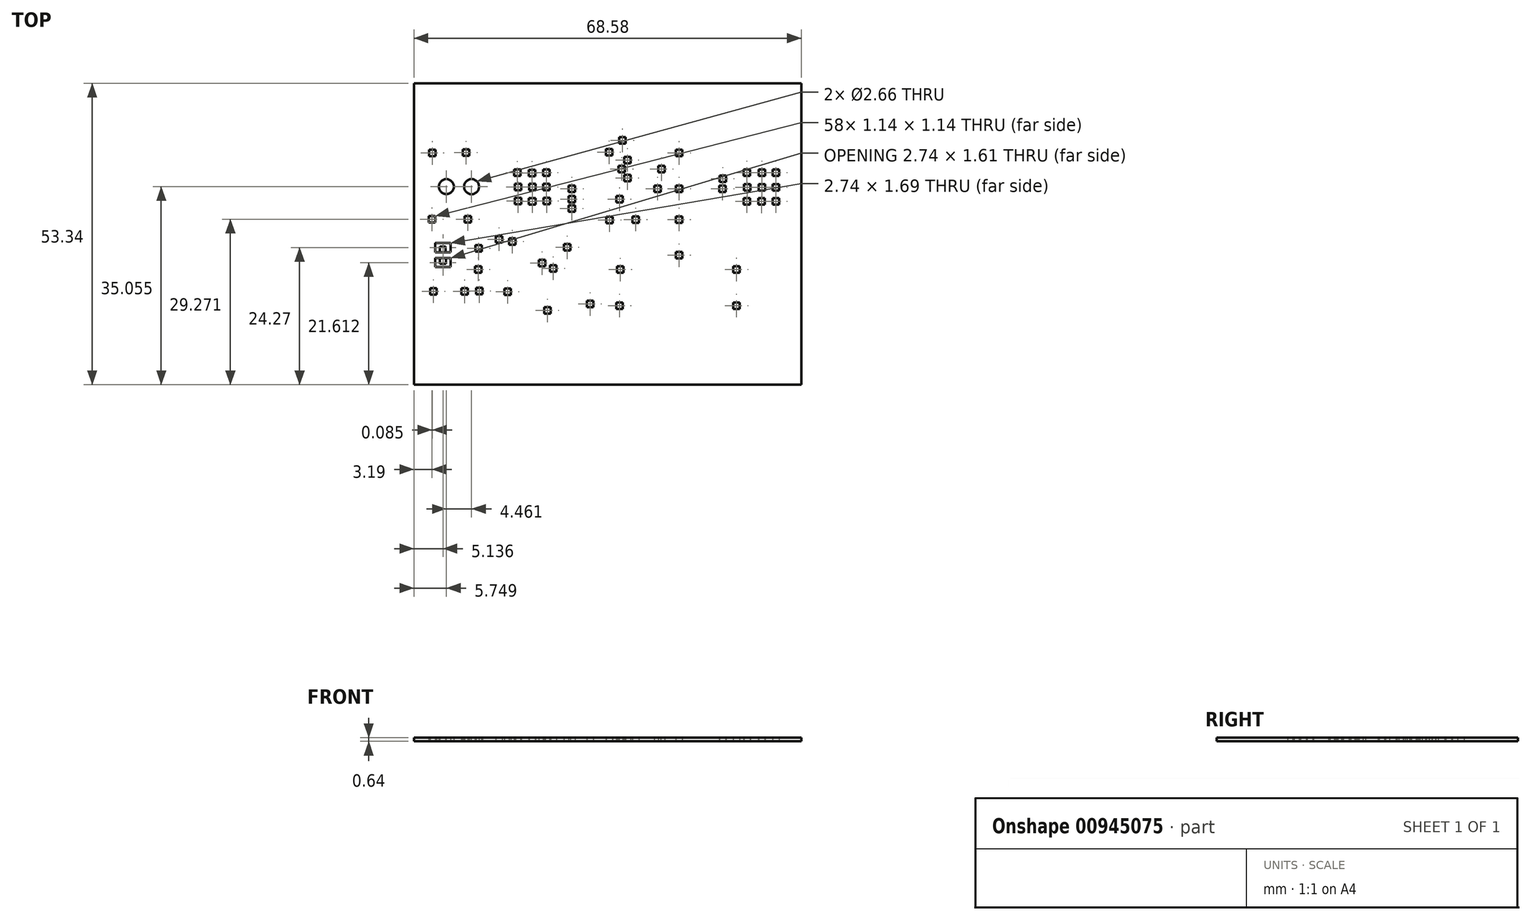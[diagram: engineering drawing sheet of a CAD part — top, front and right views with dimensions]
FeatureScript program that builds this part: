
annotation { "Feature Type Name" : "Feature", "Feature Type Description" : "" }
export const myFeature = defineFeature(function(context is Context, id is Id, definition is map)
    precondition{}
    {
        {
            var Q0;
            Q0=qCreatedBy(makeId("Top.planeOp"),FACE);
            var sketch = newSketch(context, id + "F0", { "sketchPlane" : qUnion([Q0])});
            skLineSegment(sketch, "E0.bottom", {"start": v(-43.28, 27.62) * mm, "end": v(25.3, 27.62) * mm});
            skLineSegment(sketch, "E0.top", {"start": v(-43.28, -25.72) * mm, "end": v(25.3, -25.72) * mm});
            skLineSegment(sketch, "E0.left", {"start": v(-43.28, 27.62) * mm, "end": v(-43.28, -25.72) * mm});
            skLineSegment(sketch, "E0.right", {"start": v(25.3, 27.62) * mm, "end": v(25.3, -25.72) * mm});
            skCircle(sketch, "E1", {"center": v(-37.34, -19.64) * mm, "radius": 1.71 * mm});
            skCircle(sketch, "E2", {"center": v(-37.34, -19.64) * mm, "radius": 3.05 * mm});
            skCircle(sketch, "E3", {"center": v(19.25, -19.64) * mm, "radius": 1.71 * mm});
            skCircle(sketch, "E4", {"center": v(19.25, -19.64) * mm, "radius": 3.05 * mm});
            skCircle(sketch, "E5", {"center": v(19.25, 21.73) * mm, "radius": 1.71 * mm});
            skCircle(sketch, "E6", {"center": v(19.25, 21.73) * mm, "radius": 3.05 * mm});
            skCircle(sketch, "E7", {"center": v(-37.34, 21.73) * mm, "radius": 1.71 * mm});
            skCircle(sketch, "E8", {"center": v(-37.34, 21.73) * mm, "radius": 3.05 * mm});
            skCircle(sketch, "E9", {"center": v(-37.53, 9.34) * mm, "radius": 0.82 * mm});
            skCircle(sketch, "E10", {"center": v(-37.53, 9.34) * mm, "radius": 1.33 * mm});
            skCircle(sketch, "E11", {"center": v(-33.07, 9.34) * mm, "radius": 0.83 * mm});
            skCircle(sketch, "E12", {"center": v(-33.07, 9.34) * mm, "radius": 1.33 * mm});
            skLineSegment(sketch, "E13.top", {"start": v(-39.51, -4.91) * mm, "end": v(-36.77, -4.91) * mm});
            skLineSegment(sketch, "E13.left", {"start": v(-39.51, -3.31) * mm, "end": v(-39.51, -4.91) * mm});
            skLineSegment(sketch, "E13.right", {"start": v(-36.77, -3.3) * mm, "end": v(-36.77, -4.91) * mm});
            skLineSegment(sketch, "E14.bottom", {"start": v(-38.67, -3.31) * mm, "end": v(-37.61, -3.31) * mm});
            skLineSegment(sketch, "E14.top", {"start": v(-38.67, -4.3) * mm, "end": v(-37.61, -4.3) * mm});
            skLineSegment(sketch, "E14.left", {"start": v(-38.67, -3.31) * mm, "end": v(-38.67, -4.3) * mm});
            skLineSegment(sketch, "E14.right", {"start": v(-37.61, -3.31) * mm, "end": v(-37.61, -4.3) * mm});
            skLineSegment(sketch, "E15", {"start": v(-39.51, -3.31) * mm, "end": v(-38.67, -3.31) * mm});
            skLineSegment(sketch, "E16", {"start": v(-36.77, -3.3) * mm, "end": v(-37.61, -3.31) * mm});
            skLineSegment(sketch, "E17.bottom", {"start": v(-30.19, -19.97) * mm, "end": v(-31.34, -19.97) * mm});
            skLineSegment(sketch, "E17.top", {"start": v(-30.19, -18.8) * mm, "end": v(-31.34, -18.8) * mm});
            skLineSegment(sketch, "E17.left", {"start": v(-30.19, -19.97) * mm, "end": v(-30.19, -18.8) * mm});
            skLineSegment(sketch, "E17.right", {"start": v(-31.34, -19.97) * mm, "end": v(-31.34, -18.8) * mm});
            skPoint(sketch, "E17.middle", {"position": v(-30.77, -19.39) * mm});
            skLineSegment(sketch, "E18.bottom", {"start": v(-27.6, -19.96) * mm, "end": v(-28.75, -19.96) * mm});
            skLineSegment(sketch, "E18.top", {"start": v(-27.6, -18.8) * mm, "end": v(-28.75, -18.8) * mm});
            skLineSegment(sketch, "E18.left", {"start": v(-27.6, -19.96) * mm, "end": v(-27.6, -18.8) * mm});
            skLineSegment(sketch, "E18.right", {"start": v(-28.75, -19.96) * mm, "end": v(-28.75, -18.8) * mm});
            skPoint(sketch, "E18.middle", {"position": v(-28.17, -19.39) * mm});
            skLineSegment(sketch, "E19.right", {"start": v(-29.25, -20.48) * mm, "end": v(-29.25, -18.3) * mm});
            skLineSegment(sketch, "E20.bottom", {"start": v(-24.92, -19.95) * mm, "end": v(-26.06, -19.95) * mm});
            skLineSegment(sketch, "E20.top", {"start": v(-24.92, -18.82) * mm, "end": v(-26.06, -18.82) * mm});
            skLineSegment(sketch, "E20.left", {"start": v(-24.92, -19.95) * mm, "end": v(-24.92, -18.82) * mm});
            skLineSegment(sketch, "E20.right", {"start": v(-26.06, -19.95) * mm, "end": v(-26.06, -18.82) * mm});
            skPoint(sketch, "E20.middle", {"position": v(-25.5, -19.39) * mm});
            skLineSegment(sketch, "E21.bottom", {"start": v(-22.3, -19.95) * mm, "end": v(-23.43, -19.95) * mm});
            skLineSegment(sketch, "E21.top", {"start": v(-22.3, -18.82) * mm, "end": v(-23.43, -18.82) * mm});
            skLineSegment(sketch, "E21.left", {"start": v(-22.3, -19.95) * mm, "end": v(-22.3, -18.82) * mm});
            skLineSegment(sketch, "E21.right", {"start": v(-23.43, -19.95) * mm, "end": v(-23.43, -18.82) * mm});
            skPoint(sketch, "E21.middle", {"position": v(-22.87, -19.39) * mm});
            skLineSegment(sketch, "E22.bottom", {"start": v(-19.7, -19.95) * mm, "end": v(-20.82, -19.95) * mm});
            skLineSegment(sketch, "E22.top", {"start": v(-19.7, -18.82) * mm, "end": v(-20.82, -18.82) * mm});
            skLineSegment(sketch, "E22.left", {"start": v(-19.7, -19.95) * mm, "end": v(-19.7, -18.82) * mm});
            skLineSegment(sketch, "E22.right", {"start": v(-20.82, -19.95) * mm, "end": v(-20.82, -18.82) * mm});
            skPoint(sketch, "E22.middle", {"position": v(-20.25, -19.39) * mm});
            skLineSegment(sketch, "E23.bottom", {"start": v(-17.14, -19.95) * mm, "end": v(-18.27, -19.95) * mm});
            skLineSegment(sketch, "E23.top", {"start": v(-17.14, -18.82) * mm, "end": v(-18.27, -18.82) * mm});
            skLineSegment(sketch, "E23.left", {"start": v(-17.14, -19.95) * mm, "end": v(-17.14, -18.82) * mm});
            skLineSegment(sketch, "E23.right", {"start": v(-18.27, -19.95) * mm, "end": v(-18.27, -18.82) * mm});
            skPoint(sketch, "E23.middle", {"position": v(-17.7, -19.39) * mm});
            skLineSegment(sketch, "E24.bottom", {"start": v(-14.69, -19.96) * mm, "end": v(-15.84, -19.96) * mm});
            skLineSegment(sketch, "E24.top", {"start": v(-14.69, -18.82) * mm, "end": v(-15.84, -18.82) * mm});
            skLineSegment(sketch, "E24.left", {"start": v(-14.69, -19.96) * mm, "end": v(-14.69, -18.82) * mm});
            skLineSegment(sketch, "E24.right", {"start": v(-15.84, -19.96) * mm, "end": v(-15.84, -18.82) * mm});
            skPoint(sketch, "E24.middle", {"position": v(-15.26, -19.39) * mm});
            skLineSegment(sketch, "E25.bottom", {"start": v(-12.26, -19.96) * mm, "end": v(-13.41, -19.96) * mm});
            skLineSegment(sketch, "E25.top", {"start": v(-12.26, -18.82) * mm, "end": v(-13.41, -18.82) * mm});
            skLineSegment(sketch, "E25.left", {"start": v(-12.26, -19.96) * mm, "end": v(-12.26, -18.82) * mm});
            skLineSegment(sketch, "E25.right", {"start": v(-13.41, -19.96) * mm, "end": v(-13.41, -18.82) * mm});
            skPoint(sketch, "E25.middle", {"position": v(-12.84, -19.39) * mm});
            skLineSegment(sketch, "E26.bottom", {"start": v(-30.19, -18.3) * mm, "end": v(-31.95, -18.3) * mm});
            skLineSegment(sketch, "E26.top", {"start": v(-30.19, -20.46) * mm, "end": v(-31.95, -20.46) * mm});
            skLineSegment(sketch, "E26.left", {"start": v(-30.19, -18.3) * mm, "end": v(-30.19, -20.46) * mm});
            skLineSegment(sketch, "E26.right", {"start": v(-31.95, -18.3) * mm, "end": v(-31.95, -20.46) * mm});
            skLineSegment(sketch, "E27", {"start": v(-27.6, -18.8) * mm, "end": v(-27.6, -18.3) * mm});
            skLineSegment(sketch, "E28", {"start": v(-27.6, -18.3) * mm, "end": v(-29.25, -18.3) * mm});
            skLineSegment(sketch, "E29", {"start": v(-27.6, -19.96) * mm, "end": v(-27.6, -20.47) * mm});
            skLineSegment(sketch, "E30", {"start": v(-27.6, -20.47) * mm, "end": v(-29.25, -20.48) * mm});
            skLineSegment(sketch, "E31", {"start": v(-24.92, -18.82) * mm, "end": v(-24.92, -18.32) * mm});
            skLineSegment(sketch, "E32", {"start": v(-24.92, -18.32) * mm, "end": v(-26.56, -18.32) * mm});
            skLineSegment(sketch, "E33", {"start": v(-26.56, -18.32) * mm, "end": v(-26.56, -20.47) * mm});
            skLineSegment(sketch, "E34", {"start": v(-26.56, -20.47) * mm, "end": v(-24.92, -20.47) * mm});
            skLineSegment(sketch, "E35", {"start": v(-24.92, -20.47) * mm, "end": v(-24.92, -19.95) * mm});
            skLineSegment(sketch, "E36", {"start": v(-22.3, -18.82) * mm, "end": v(-22.3, -18.32) * mm});
            skLineSegment(sketch, "E37", {"start": v(-22.3, -18.32) * mm, "end": v(-23.96, -18.32) * mm});
            skLineSegment(sketch, "E38", {"start": v(-23.96, -18.32) * mm, "end": v(-23.96, -20.47) * mm});
            skLineSegment(sketch, "E39", {"start": v(-23.96, -20.47) * mm, "end": v(-22.3, -20.47) * mm});
            skLineSegment(sketch, "E40", {"start": v(-22.3, -20.47) * mm, "end": v(-22.3, -19.95) * mm});
            skLineSegment(sketch, "E41", {"start": v(-19.7, -18.82) * mm, "end": v(-19.7, -18.32) * mm});
            skLineSegment(sketch, "E42", {"start": v(-19.7, -18.32) * mm, "end": v(-21.35, -18.32) * mm});
            skLineSegment(sketch, "E43", {"start": v(-21.35, -18.32) * mm, "end": v(-21.35, -20.46) * mm});
            skLineSegment(sketch, "E44", {"start": v(-21.35, -20.46) * mm, "end": v(-19.7, -20.46) * mm});
            skLineSegment(sketch, "E45", {"start": v(-19.7, -20.46) * mm, "end": v(-19.7, -19.95) * mm});
            skLineSegment(sketch, "E46", {"start": v(-17.14, -18.82) * mm, "end": v(-17.14, -18.3) * mm});
            skLineSegment(sketch, "E47", {"start": v(-17.14, -18.3) * mm, "end": v(-18.8, -18.3) * mm});
            skLineSegment(sketch, "E48", {"start": v(-18.8, -18.3) * mm, "end": v(-18.8, -20.46) * mm});
            skLineSegment(sketch, "E49", {"start": v(-18.8, -20.46) * mm, "end": v(-17.14, -20.46) * mm});
            skLineSegment(sketch, "E50", {"start": v(-17.14, -20.46) * mm, "end": v(-17.14, -19.95) * mm});
            skLineSegment(sketch, "E51", {"start": v(-14.69, -18.82) * mm, "end": v(-14.69, -18.3) * mm});
            skLineSegment(sketch, "E52", {"start": v(-14.69, -18.3) * mm, "end": v(-16.33, -18.3) * mm});
            skLineSegment(sketch, "E53", {"start": v(-16.33, -18.3) * mm, "end": v(-16.33, -20.47) * mm});
            skLineSegment(sketch, "E54", {"start": v(-16.33, -20.47) * mm, "end": v(-14.69, -20.47) * mm});
            skLineSegment(sketch, "E55", {"start": v(-14.69, -20.47) * mm, "end": v(-14.69, -19.96) * mm});
            skLineSegment(sketch, "E56", {"start": v(-12.26, -18.82) * mm, "end": v(-12.26, -18.31) * mm});
            skLineSegment(sketch, "E57", {"start": v(-12.26, -18.31) * mm, "end": v(-13.91, -18.31) * mm});
            skLineSegment(sketch, "E58", {"start": v(-13.91, -18.31) * mm, "end": v(-13.91, -20.47) * mm});
            skLineSegment(sketch, "E59", {"start": v(-13.91, -20.47) * mm, "end": v(-12.26, -20.47) * mm});
            skLineSegment(sketch, "E60", {"start": v(-12.26, -20.47) * mm, "end": v(-12.26, -19.96) * mm});
            skLineSegment(sketch, "E61.bottom", {"start": v(-9.74, -19.95) * mm, "end": v(-10.89, -19.95) * mm});
            skLineSegment(sketch, "E61.top", {"start": v(-9.74, -18.82) * mm, "end": v(-10.89, -18.82) * mm});
            skLineSegment(sketch, "E61.left", {"start": v(-9.74, -19.95) * mm, "end": v(-9.74, -18.82) * mm});
            skLineSegment(sketch, "E61.right", {"start": v(-10.89, -19.95) * mm, "end": v(-10.89, -18.82) * mm});
            skPoint(sketch, "E61.middle", {"position": v(-10.31, -19.39) * mm});
            skPoint(sketch, "E62.middle", {"position": v(-7.76, -19.39) * mm});
            skLineSegment(sketch, "E63.bottom", {"start": v(-7.19, -19.96) * mm, "end": v(-8.34, -19.96) * mm});
            skLineSegment(sketch, "E63.top", {"start": v(-7.19, -18.81) * mm, "end": v(-8.34, -18.81) * mm});
            skLineSegment(sketch, "E63.left", {"start": v(-7.19, -19.96) * mm, "end": v(-7.19, -18.81) * mm});
            skLineSegment(sketch, "E63.right", {"start": v(-8.34, -19.96) * mm, "end": v(-8.34, -18.81) * mm});
            skLineSegment(sketch, "E64.bottom", {"start": v(-4.68, -19.96) * mm, "end": v(-5.82, -19.96) * mm});
            skLineSegment(sketch, "E64.top", {"start": v(-4.68, -18.81) * mm, "end": v(-5.82, -18.81) * mm});
            skLineSegment(sketch, "E64.left", {"start": v(-4.68, -19.96) * mm, "end": v(-4.68, -18.81) * mm});
            skLineSegment(sketch, "E64.right", {"start": v(-5.82, -19.96) * mm, "end": v(-5.82, -18.81) * mm});
            skPoint(sketch, "E64.middle", {"position": v(-5.25, -19.39) * mm});
            skLineSegment(sketch, "E65.bottom", {"start": v(-2.14, -19.96) * mm, "end": v(-3.29, -19.96) * mm});
            skLineSegment(sketch, "E65.top", {"start": v(-2.14, -18.81) * mm, "end": v(-3.29, -18.81) * mm});
            skLineSegment(sketch, "E65.left", {"start": v(-2.14, -19.96) * mm, "end": v(-2.14, -18.81) * mm});
            skLineSegment(sketch, "E65.right", {"start": v(-3.29, -19.96) * mm, "end": v(-3.29, -18.81) * mm});
            skPoint(sketch, "E65.middle", {"position": v(-2.71, -19.39) * mm});
            skLineSegment(sketch, "E66.bottom", {"start": v(0.38, -19.96) * mm, "end": v(-0.76, -19.96) * mm});
            skLineSegment(sketch, "E66.top", {"start": v(0.38, -18.81) * mm, "end": v(-0.76, -18.81) * mm});
            skLineSegment(sketch, "E66.left", {"start": v(0.38, -19.96) * mm, "end": v(0.38, -18.81) * mm});
            skLineSegment(sketch, "E66.right", {"start": v(-0.76, -19.96) * mm, "end": v(-0.76, -18.81) * mm});
            skPoint(sketch, "E66.middle", {"position": v(-0.19, -19.39) * mm});
            skLineSegment(sketch, "E67.bottom", {"start": v(2.91, -19.96) * mm, "end": v(1.78, -19.96) * mm});
            skLineSegment(sketch, "E67.top", {"start": v(2.91, -18.81) * mm, "end": v(1.78, -18.81) * mm});
            skLineSegment(sketch, "E67.left", {"start": v(2.91, -19.96) * mm, "end": v(2.91, -18.81) * mm});
            skLineSegment(sketch, "E67.right", {"start": v(1.78, -19.96) * mm, "end": v(1.78, -18.81) * mm});
            skPoint(sketch, "E67.middle", {"position": v(2.35, -19.39) * mm});
            skLineSegment(sketch, "E68.bottom", {"start": v(8.82, -19.96) * mm, "end": v(7.68, -19.96) * mm});
            skLineSegment(sketch, "E68.top", {"start": v(8.82, -18.81) * mm, "end": v(7.68, -18.81) * mm});
            skLineSegment(sketch, "E68.left", {"start": v(8.82, -19.96) * mm, "end": v(8.82, -18.81) * mm});
            skLineSegment(sketch, "E68.right", {"start": v(7.68, -19.96) * mm, "end": v(7.68, -18.81) * mm});
            skPoint(sketch, "E68.middle", {"position": v(8.25, -19.39) * mm});
            skLineSegment(sketch, "E69.bottom", {"start": v(11.35, -19.96) * mm, "end": v(10.21, -19.96) * mm});
            skLineSegment(sketch, "E69.top", {"start": v(11.35, -18.81) * mm, "end": v(10.21, -18.81) * mm});
            skLineSegment(sketch, "E69.left", {"start": v(11.35, -19.96) * mm, "end": v(11.35, -18.81) * mm});
            skLineSegment(sketch, "E69.right", {"start": v(10.21, -19.96) * mm, "end": v(10.21, -18.81) * mm});
            skPoint(sketch, "E69.middle", {"position": v(10.78, -19.39) * mm});
            skPoint(sketch, "E70.middle", {"position": v(13.33, -19.39) * mm});
            skLineSegment(sketch, "E71.bottom", {"start": v(13.9, -19.96) * mm, "end": v(12.75, -19.96) * mm});
            skLineSegment(sketch, "E71.top", {"start": v(13.9, -18.82) * mm, "end": v(12.75, -18.82) * mm});
            skLineSegment(sketch, "E71.left", {"start": v(13.9, -19.96) * mm, "end": v(13.9, -18.82) * mm});
            skLineSegment(sketch, "E71.right", {"start": v(12.75, -19.96) * mm, "end": v(12.75, -18.82) * mm});
            skLineSegment(sketch, "E72", {"start": v(-9.74, -18.82) * mm, "end": v(-9.74, -18.3) * mm});
            skLineSegment(sketch, "E73", {"start": v(-9.74, -18.3) * mm, "end": v(-11.39, -18.3) * mm});
            skLineSegment(sketch, "E74", {"start": v(-11.39, -18.3) * mm, "end": v(-11.39, -20.46) * mm});
            skLineSegment(sketch, "E75", {"start": v(-11.39, -20.46) * mm, "end": v(-9.74, -20.46) * mm});
            skLineSegment(sketch, "E76", {"start": v(-9.74, -20.46) * mm, "end": v(-9.74, -19.95) * mm});
            skLineSegment(sketch, "E77", {"start": v(-7.19, -18.81) * mm, "end": v(-7.19, -18.3) * mm});
            skLineSegment(sketch, "E78", {"start": v(-7.19, -18.3) * mm, "end": v(-8.84, -18.3) * mm});
            skLineSegment(sketch, "E79", {"start": v(-8.84, -18.3) * mm, "end": v(-8.84, -20.46) * mm});
            skLineSegment(sketch, "E80", {"start": v(-8.84, -20.46) * mm, "end": v(-7.19, -20.46) * mm});
            skLineSegment(sketch, "E81", {"start": v(-7.19, -20.46) * mm, "end": v(-7.19, -19.96) * mm});
            skLineSegment(sketch, "E82", {"start": v(-4.68, -18.81) * mm, "end": v(-4.68, -18.3) * mm});
            skLineSegment(sketch, "E83", {"start": v(-4.68, -18.3) * mm, "end": v(-6.32, -18.3) * mm});
            skLineSegment(sketch, "E84", {"start": v(-6.32, -18.3) * mm, "end": v(-6.32, -20.46) * mm});
            skLineSegment(sketch, "E85", {"start": v(-6.32, -20.46) * mm, "end": v(-4.68, -20.46) * mm});
            skLineSegment(sketch, "E86", {"start": v(-4.68, -20.46) * mm, "end": v(-4.68, -19.96) * mm});
            skLineSegment(sketch, "E87", {"start": v(-2.14, -18.81) * mm, "end": v(-2.14, -18.3) * mm});
            skLineSegment(sketch, "E88", {"start": v(-2.14, -18.3) * mm, "end": v(-3.8, -18.3) * mm});
            skLineSegment(sketch, "E89", {"start": v(-3.8, -18.3) * mm, "end": v(-3.78, -20.45) * mm});
            skLineSegment(sketch, "E90", {"start": v(-3.78, -20.45) * mm, "end": v(-2.14, -20.45) * mm});
            skLineSegment(sketch, "E91", {"start": v(-2.14, -20.45) * mm, "end": v(-2.14, -19.96) * mm});
            skLineSegment(sketch, "E92", {"start": v(0.38, -18.81) * mm, "end": v(0.38, -18.3) * mm});
            skLineSegment(sketch, "E93", {"start": v(0.38, -18.3) * mm, "end": v(-1.26, -18.3) * mm});
            skLineSegment(sketch, "E94", {"start": v(-1.26, -18.3) * mm, "end": v(-1.26, -20.46) * mm});
            skLineSegment(sketch, "E95", {"start": v(-1.26, -20.46) * mm, "end": v(0.38, -20.46) * mm});
            skLineSegment(sketch, "E96", {"start": v(0.38, -20.46) * mm, "end": v(0.38, -19.96) * mm});
            skLineSegment(sketch, "E97", {"start": v(2.91, -18.81) * mm, "end": v(2.91, -18.31) * mm});
            skLineSegment(sketch, "E98", {"start": v(2.91, -18.31) * mm, "end": v(1.27, -18.31) * mm});
            skLineSegment(sketch, "E99", {"start": v(1.27, -18.31) * mm, "end": v(1.27, -20.48) * mm});
            skLineSegment(sketch, "E100", {"start": v(1.27, -20.48) * mm, "end": v(2.91, -20.48) * mm});
            skLineSegment(sketch, "E101", {"start": v(2.91, -20.48) * mm, "end": v(2.91, -19.96) * mm});
            skLineSegment(sketch, "E102", {"start": v(8.82, -18.81) * mm, "end": v(8.82, -18.3) * mm});
            skLineSegment(sketch, "E103", {"start": v(8.82, -18.3) * mm, "end": v(7.17, -18.3) * mm});
            skLineSegment(sketch, "E104", {"start": v(7.17, -18.3) * mm, "end": v(7.17, -20.46) * mm});
            skLineSegment(sketch, "E105", {"start": v(7.17, -20.46) * mm, "end": v(8.82, -20.46) * mm});
            skLineSegment(sketch, "E106", {"start": v(8.82, -20.46) * mm, "end": v(8.82, -19.96) * mm});
            skLineSegment(sketch, "E107", {"start": v(11.35, -18.81) * mm, "end": v(11.35, -18.3) * mm});
            skLineSegment(sketch, "E108", {"start": v(11.35, -18.3) * mm, "end": v(9.7, -18.3) * mm});
            skLineSegment(sketch, "E109", {"start": v(9.7, -18.3) * mm, "end": v(9.7, -20.46) * mm});
            skLineSegment(sketch, "E110", {"start": v(9.7, -20.46) * mm, "end": v(11.35, -20.46) * mm});
            skLineSegment(sketch, "E111", {"start": v(11.35, -20.46) * mm, "end": v(11.35, -19.96) * mm});
            skLineSegment(sketch, "E112", {"start": v(13.9, -18.82) * mm, "end": v(13.9, -18.31) * mm});
            skLineSegment(sketch, "E113", {"start": v(13.9, -18.31) * mm, "end": v(12.25, -18.31) * mm});
            skLineSegment(sketch, "E114", {"start": v(12.25, -18.31) * mm, "end": v(12.25, -20.46) * mm});
            skLineSegment(sketch, "E115", {"start": v(12.25, -20.46) * mm, "end": v(13.9, -20.46) * mm});
            skLineSegment(sketch, "E116", {"start": v(13.9, -20.46) * mm, "end": v(13.9, -19.96) * mm});
            skLineSegment(sketch, "E117.bottom", {"start": v(11.36, 20.51) * mm, "end": v(10.21, 20.51) * mm});
            skLineSegment(sketch, "E117.top", {"start": v(11.36, 21.64) * mm, "end": v(10.21, 21.64) * mm});
            skLineSegment(sketch, "E117.left", {"start": v(11.36, 20.51) * mm, "end": v(11.36, 21.64) * mm});
            skLineSegment(sketch, "E117.right", {"start": v(10.21, 20.51) * mm, "end": v(10.21, 21.64) * mm});
            skPoint(sketch, "E117.middle", {"position": v(10.78, 21.08) * mm});
            skLineSegment(sketch, "E118.bottom", {"start": v(8.82, 20.51) * mm, "end": v(7.68, 20.51) * mm});
            skLineSegment(sketch, "E118.top", {"start": v(8.82, 21.64) * mm, "end": v(7.68, 21.64) * mm});
            skLineSegment(sketch, "E118.left", {"start": v(8.82, 20.51) * mm, "end": v(8.82, 21.64) * mm});
            skLineSegment(sketch, "E118.right", {"start": v(7.68, 20.51) * mm, "end": v(7.68, 21.64) * mm});
            skPoint(sketch, "E118.middle", {"position": v(8.25, 21.08) * mm});
            skLineSegment(sketch, "E119.bottom", {"start": v(2.92, 20.51) * mm, "end": v(1.77, 20.51) * mm});
            skLineSegment(sketch, "E119.top", {"start": v(2.92, 21.64) * mm, "end": v(1.77, 21.64) * mm});
            skLineSegment(sketch, "E119.left", {"start": v(2.92, 20.51) * mm, "end": v(2.92, 21.64) * mm});
            skLineSegment(sketch, "E119.right", {"start": v(1.77, 20.51) * mm, "end": v(1.77, 21.64) * mm});
            skPoint(sketch, "E119.middle", {"position": v(2.35, 21.08) * mm});
            skLineSegment(sketch, "E120.bottom", {"start": v(0.39, 20.5) * mm, "end": v(-0.76, 20.5) * mm});
            skLineSegment(sketch, "E120.top", {"start": v(0.39, 21.64) * mm, "end": v(-0.76, 21.64) * mm});
            skLineSegment(sketch, "E120.left", {"start": v(0.39, 20.5) * mm, "end": v(0.39, 21.64) * mm});
            skLineSegment(sketch, "E120.right", {"start": v(-0.76, 20.5) * mm, "end": v(-0.76, 21.64) * mm});
            skPoint(sketch, "E120.middle", {"position": v(-0.19, 21.08) * mm});
            skLineSegment(sketch, "E121.bottom", {"start": v(-2.14, 20.5) * mm, "end": v(-3.29, 20.5) * mm});
            skLineSegment(sketch, "E121.top", {"start": v(-2.14, 21.65) * mm, "end": v(-3.29, 21.65) * mm});
            skLineSegment(sketch, "E121.left", {"start": v(-2.14, 20.5) * mm, "end": v(-2.14, 21.65) * mm});
            skLineSegment(sketch, "E121.right", {"start": v(-3.29, 20.5) * mm, "end": v(-3.29, 21.65) * mm});
            skPoint(sketch, "E121.middle", {"position": v(-2.71, 21.08) * mm});
            skLineSegment(sketch, "E122.bottom", {"start": v(-4.68, 20.5) * mm, "end": v(-5.82, 20.5) * mm});
            skLineSegment(sketch, "E122.top", {"start": v(-4.68, 21.65) * mm, "end": v(-5.82, 21.65) * mm});
            skLineSegment(sketch, "E122.left", {"start": v(-4.68, 20.5) * mm, "end": v(-4.68, 21.65) * mm});
            skLineSegment(sketch, "E122.right", {"start": v(-5.82, 20.5) * mm, "end": v(-5.82, 21.65) * mm});
            skPoint(sketch, "E122.middle", {"position": v(-5.25, 21.08) * mm});
            skLineSegment(sketch, "E123.bottom", {"start": v(-7.2, 20.5) * mm, "end": v(-8.33, 20.5) * mm});
            skLineSegment(sketch, "E123.top", {"start": v(-7.2, 21.65) * mm, "end": v(-8.33, 21.65) * mm});
            skLineSegment(sketch, "E123.left", {"start": v(-7.2, 20.5) * mm, "end": v(-7.2, 21.65) * mm});
            skLineSegment(sketch, "E123.right", {"start": v(-8.33, 20.5) * mm, "end": v(-8.33, 21.65) * mm});
            skPoint(sketch, "E123.middle", {"position": v(-7.76, 21.08) * mm});
            skLineSegment(sketch, "E124.bottom", {"start": v(-9.74, 20.5) * mm, "end": v(-10.88, 20.5) * mm});
            skLineSegment(sketch, "E124.top", {"start": v(-9.74, 21.64) * mm, "end": v(-10.88, 21.64) * mm});
            skLineSegment(sketch, "E124.left", {"start": v(-9.74, 20.5) * mm, "end": v(-9.74, 21.64) * mm});
            skLineSegment(sketch, "E124.right", {"start": v(-10.88, 20.5) * mm, "end": v(-10.88, 21.64) * mm});
            skPoint(sketch, "E124.middle", {"position": v(-10.31, 21.08) * mm});
            skLineSegment(sketch, "E125.bottom", {"start": v(-12.26, 20.51) * mm, "end": v(-13.41, 20.51) * mm});
            skLineSegment(sketch, "E125.top", {"start": v(-12.26, 21.64) * mm, "end": v(-13.41, 21.64) * mm});
            skLineSegment(sketch, "E125.left", {"start": v(-12.26, 20.51) * mm, "end": v(-12.26, 21.64) * mm});
            skLineSegment(sketch, "E125.right", {"start": v(-13.41, 20.51) * mm, "end": v(-13.41, 21.64) * mm});
            skPoint(sketch, "E125.middle", {"position": v(-12.84, 21.08) * mm});
            skLineSegment(sketch, "E126.bottom", {"start": v(-14.7, 20.5) * mm, "end": v(-15.83, 20.5) * mm});
            skLineSegment(sketch, "E126.top", {"start": v(-14.7, 21.65) * mm, "end": v(-15.83, 21.65) * mm});
            skLineSegment(sketch, "E126.left", {"start": v(-14.7, 20.5) * mm, "end": v(-14.7, 21.65) * mm});
            skLineSegment(sketch, "E126.right", {"start": v(-15.83, 20.5) * mm, "end": v(-15.83, 21.65) * mm});
            skPoint(sketch, "E126.middle", {"position": v(-15.26, 21.08) * mm});
            skLineSegment(sketch, "E127.bottom", {"start": v(-17.13, 20.5) * mm, "end": v(-18.28, 20.5) * mm});
            skLineSegment(sketch, "E127.top", {"start": v(-17.13, 21.65) * mm, "end": v(-18.28, 21.65) * mm});
            skLineSegment(sketch, "E127.left", {"start": v(-17.13, 20.5) * mm, "end": v(-17.13, 21.65) * mm});
            skLineSegment(sketch, "E127.right", {"start": v(-18.28, 20.5) * mm, "end": v(-18.28, 21.65) * mm});
            skPoint(sketch, "E127.middle", {"position": v(-17.7, 21.08) * mm});
            skLineSegment(sketch, "E128.bottom", {"start": v(-19.69, 20.5) * mm, "end": v(-20.82, 20.5) * mm});
            skLineSegment(sketch, "E128.top", {"start": v(-19.69, 21.65) * mm, "end": v(-20.82, 21.65) * mm});
            skLineSegment(sketch, "E128.left", {"start": v(-19.69, 20.5) * mm, "end": v(-19.69, 21.65) * mm});
            skLineSegment(sketch, "E128.right", {"start": v(-20.82, 20.5) * mm, "end": v(-20.82, 21.65) * mm});
            skPoint(sketch, "E128.middle", {"position": v(-20.25, 21.08) * mm});
            skLineSegment(sketch, "E129.bottom", {"start": v(-22.29, 20.5) * mm, "end": v(-23.44, 20.5) * mm});
            skLineSegment(sketch, "E129.top", {"start": v(-22.29, 21.65) * mm, "end": v(-23.44, 21.65) * mm});
            skLineSegment(sketch, "E129.left", {"start": v(-22.29, 20.5) * mm, "end": v(-22.29, 21.65) * mm});
            skLineSegment(sketch, "E129.right", {"start": v(-23.44, 20.5) * mm, "end": v(-23.44, 21.65) * mm});
            skPoint(sketch, "E129.middle", {"position": v(-22.87, 21.08) * mm});
            skLineSegment(sketch, "E130.bottom", {"start": v(-24.92, 20.5) * mm, "end": v(-26.06, 20.5) * mm});
            skLineSegment(sketch, "E130.top", {"start": v(-24.92, 21.65) * mm, "end": v(-26.06, 21.65) * mm});
            skLineSegment(sketch, "E130.left", {"start": v(-24.92, 20.5) * mm, "end": v(-24.92, 21.65) * mm});
            skLineSegment(sketch, "E130.right", {"start": v(-26.06, 20.5) * mm, "end": v(-26.06, 21.65) * mm});
            skPoint(sketch, "E130.middle", {"position": v(-25.5, 21.08) * mm});
            skLineSegment(sketch, "E131.bottom", {"start": v(-27.6, 20.5) * mm, "end": v(-28.74, 20.5) * mm});
            skLineSegment(sketch, "E131.top", {"start": v(-27.6, 21.65) * mm, "end": v(-28.74, 21.65) * mm});
            skLineSegment(sketch, "E131.left", {"start": v(-27.6, 20.5) * mm, "end": v(-27.6, 21.65) * mm});
            skLineSegment(sketch, "E131.right", {"start": v(-28.74, 20.5) * mm, "end": v(-28.74, 21.65) * mm});
            skPoint(sketch, "E131.middle", {"position": v(-28.17, 21.08) * mm});
            skLineSegment(sketch, "E132.bottom", {"start": v(13.9, 20.5) * mm, "end": v(12.76, 20.5) * mm});
            skLineSegment(sketch, "E132.top", {"start": v(13.9, 21.65) * mm, "end": v(12.76, 21.65) * mm});
            skLineSegment(sketch, "E132.left", {"start": v(13.9, 20.5) * mm, "end": v(13.9, 21.65) * mm});
            skLineSegment(sketch, "E132.right", {"start": v(12.76, 20.5) * mm, "end": v(12.76, 21.65) * mm});
            skPoint(sketch, "E132.middle", {"position": v(13.33, 21.08) * mm});
            skLineSegment(sketch, "E133", {"start": v(13.9, 21.65) * mm, "end": v(13.9, 22.15) * mm});
            skLineSegment(sketch, "E134", {"start": v(13.9, 22.15) * mm, "end": v(12.25, 22.15) * mm});
            skLineSegment(sketch, "E135", {"start": v(12.25, 22.15) * mm, "end": v(12.25, 19.98) * mm});
            skLineSegment(sketch, "E136", {"start": v(12.25, 19.98) * mm, "end": v(13.9, 19.98) * mm});
            skLineSegment(sketch, "E137", {"start": v(13.9, 19.98) * mm, "end": v(13.9, 20.5) * mm});
            skLineSegment(sketch, "E138.bottom", {"start": v(-30.2, 20.5) * mm, "end": v(-31.34, 20.5) * mm});
            skLineSegment(sketch, "E138.top", {"start": v(-30.2, 21.64) * mm, "end": v(-31.34, 21.64) * mm});
            skLineSegment(sketch, "E138.left", {"start": v(-30.2, 20.5) * mm, "end": v(-30.2, 21.64) * mm});
            skLineSegment(sketch, "E138.right", {"start": v(-31.34, 20.5) * mm, "end": v(-31.34, 21.64) * mm});
            skPoint(sketch, "E138.middle", {"position": v(-30.77, 21.08) * mm});
            skLineSegment(sketch, "E139", {"start": v(-30.2, 21.64) * mm, "end": v(-30.2, 22.15) * mm});
            skLineSegment(sketch, "E140", {"start": v(-30.2, 22.15) * mm, "end": v(-31.85, 22.15) * mm});
            skLineSegment(sketch, "E141", {"start": v(-31.85, 22.15) * mm, "end": v(-31.85, 19.99) * mm});
            skLineSegment(sketch, "E142", {"start": v(-31.85, 19.99) * mm, "end": v(-30.2, 19.99) * mm});
            skLineSegment(sketch, "E143", {"start": v(-30.2, 19.99) * mm, "end": v(-30.2, 20.5) * mm});
            skLineSegment(sketch, "E144", {"start": v(-27.6, 21.65) * mm, "end": v(-27.6, 22.15) * mm});
            skLineSegment(sketch, "E145", {"start": v(-27.6, 22.15) * mm, "end": v(-29.25, 22.15) * mm});
            skLineSegment(sketch, "E146", {"start": v(-29.25, 22.15) * mm, "end": v(-29.25, 20) * mm});
            skLineSegment(sketch, "E147", {"start": v(-29.25, 20) * mm, "end": v(-27.6, 20) * mm});
            skLineSegment(sketch, "E148", {"start": v(-27.6, 20) * mm, "end": v(-27.6, 20.5) * mm});
            skLineSegment(sketch, "E149", {"start": v(-24.92, 21.65) * mm, "end": v(-24.92, 22.15) * mm});
            skLineSegment(sketch, "E150", {"start": v(-24.92, 22.15) * mm, "end": v(-26.57, 22.15) * mm});
            skLineSegment(sketch, "E151", {"start": v(-26.57, 22.15) * mm, "end": v(-26.57, 19.98) * mm});
            skLineSegment(sketch, "E152", {"start": v(-26.57, 19.98) * mm, "end": v(-24.92, 19.98) * mm});
            skLineSegment(sketch, "E153", {"start": v(-24.92, 19.98) * mm, "end": v(-24.92, 20.5) * mm});
            skLineSegment(sketch, "E154", {"start": v(-22.29, 21.65) * mm, "end": v(-22.29, 22.15) * mm});
            skLineSegment(sketch, "E155", {"start": v(-22.29, 22.15) * mm, "end": v(-23.93, 22.15) * mm});
            skLineSegment(sketch, "E156", {"start": v(-23.93, 22.15) * mm, "end": v(-23.93, 19.98) * mm});
            skLineSegment(sketch, "E157", {"start": v(-23.93, 19.98) * mm, "end": v(-22.29, 19.98) * mm});
            skLineSegment(sketch, "E158", {"start": v(-22.29, 19.98) * mm, "end": v(-22.29, 20.5) * mm});
            skLineSegment(sketch, "E159", {"start": v(-19.69, 21.65) * mm, "end": v(-19.69, 22.14) * mm});
            skLineSegment(sketch, "E160", {"start": v(-19.69, 22.14) * mm, "end": v(-21.33, 22.14) * mm});
            skLineSegment(sketch, "E161", {"start": v(-21.33, 22.14) * mm, "end": v(-21.33, 19.99) * mm});
            skLineSegment(sketch, "E162", {"start": v(-21.33, 19.99) * mm, "end": v(-19.69, 19.99) * mm});
            skLineSegment(sketch, "E163", {"start": v(-19.69, 19.99) * mm, "end": v(-19.69, 20.5) * mm});
            skLineSegment(sketch, "E164", {"start": v(-17.13, 21.65) * mm, "end": v(-17.13, 22.15) * mm});
            skLineSegment(sketch, "E165", {"start": v(-17.13, 22.15) * mm, "end": v(-18.76, 22.15) * mm});
            skLineSegment(sketch, "E166", {"start": v(-18.76, 22.15) * mm, "end": v(-18.76, 19.98) * mm});
            skLineSegment(sketch, "E167", {"start": v(-18.76, 19.98) * mm, "end": v(-17.13, 19.98) * mm});
            skLineSegment(sketch, "E168", {"start": v(-17.13, 19.98) * mm, "end": v(-17.13, 20.5) * mm});
            skLineSegment(sketch, "E169", {"start": v(-14.7, 21.65) * mm, "end": v(-14.7, 22.17) * mm});
            skLineSegment(sketch, "E170", {"start": v(-14.7, 22.17) * mm, "end": v(-16.33, 22.17) * mm});
            skLineSegment(sketch, "E171", {"start": v(-16.33, 22.17) * mm, "end": v(-16.33, 20.02) * mm});
            skLineSegment(sketch, "E172", {"start": v(-16.33, 20.02) * mm, "end": v(-14.7, 20.02) * mm});
            skLineSegment(sketch, "E173", {"start": v(-14.7, 20.02) * mm, "end": v(-14.7, 20.5) * mm});
            skLineSegment(sketch, "E174", {"start": v(-12.26, 21.64) * mm, "end": v(-12.26, 22.14) * mm});
            skLineSegment(sketch, "E175", {"start": v(-12.26, 22.14) * mm, "end": v(-13.9, 22.14) * mm});
            skLineSegment(sketch, "E176", {"start": v(-13.9, 22.14) * mm, "end": v(-13.9, 20) * mm});
            skLineSegment(sketch, "E177", {"start": v(-13.9, 20) * mm, "end": v(-12.26, 20) * mm});
            skLineSegment(sketch, "E178", {"start": v(-12.26, 20) * mm, "end": v(-12.26, 20.51) * mm});
            skLineSegment(sketch, "E179", {"start": v(-9.74, 21.64) * mm, "end": v(-9.74, 22.16) * mm});
            skLineSegment(sketch, "E180", {"start": v(-9.74, 22.16) * mm, "end": v(-11.4, 22.16) * mm});
            skLineSegment(sketch, "E181", {"start": v(-11.4, 22.16) * mm, "end": v(-11.4, 20) * mm});
            skLineSegment(sketch, "E182", {"start": v(-11.4, 20) * mm, "end": v(-9.74, 20) * mm});
            skLineSegment(sketch, "E183", {"start": v(-9.74, 20) * mm, "end": v(-9.74, 20.5) * mm});
            skLineSegment(sketch, "E184", {"start": v(-7.2, 21.65) * mm, "end": v(-7.2, 22.16) * mm});
            skLineSegment(sketch, "E185", {"start": v(-7.2, 22.16) * mm, "end": v(-8.84, 22.16) * mm});
            skLineSegment(sketch, "E186", {"start": v(-8.84, 22.16) * mm, "end": v(-8.84, 20) * mm});
            skLineSegment(sketch, "E187", {"start": v(-8.84, 20) * mm, "end": v(-7.2, 20) * mm});
            skLineSegment(sketch, "E188", {"start": v(-7.2, 20) * mm, "end": v(-7.2, 20.5) * mm});
            skLineSegment(sketch, "E189", {"start": v(-4.68, 21.65) * mm, "end": v(-4.68, 22.16) * mm});
            skLineSegment(sketch, "E190", {"start": v(-4.68, 22.16) * mm, "end": v(-6.34, 22.16) * mm});
            skLineSegment(sketch, "E191", {"start": v(-6.34, 22.16) * mm, "end": v(-6.34, 20) * mm});
            skLineSegment(sketch, "E192", {"start": v(-6.34, 20) * mm, "end": v(-4.68, 20) * mm});
            skLineSegment(sketch, "E193", {"start": v(-4.68, 20) * mm, "end": v(-4.68, 20.5) * mm});
            skLineSegment(sketch, "E194", {"start": v(-2.14, 21.65) * mm, "end": v(-2.14, 22.16) * mm});
            skLineSegment(sketch, "E195", {"start": v(-2.14, 22.16) * mm, "end": v(-3.8, 22.16) * mm});
            skLineSegment(sketch, "E196", {"start": v(-3.8, 22.16) * mm, "end": v(-3.8, 20) * mm});
            skLineSegment(sketch, "E197", {"start": v(-3.8, 20) * mm, "end": v(-2.14, 20) * mm});
            skLineSegment(sketch, "E198", {"start": v(-2.14, 20) * mm, "end": v(-2.14, 20.5) * mm});
            skLineSegment(sketch, "E199", {"start": v(0.39, 21.64) * mm, "end": v(0.39, 22.16) * mm});
            skLineSegment(sketch, "E200", {"start": v(0.39, 22.16) * mm, "end": v(-1.26, 22.16) * mm});
            skLineSegment(sketch, "E201", {"start": v(-1.26, 22.16) * mm, "end": v(-1.26, 20) * mm});
            skLineSegment(sketch, "E202", {"start": v(-1.26, 20) * mm, "end": v(0.39, 20) * mm});
            skLineSegment(sketch, "E203", {"start": v(0.39, 20) * mm, "end": v(0.39, 20.5) * mm});
            skLineSegment(sketch, "E204", {"start": v(2.92, 21.64) * mm, "end": v(2.92, 22.16) * mm});
            skLineSegment(sketch, "E205", {"start": v(2.92, 22.16) * mm, "end": v(1.27, 22.16) * mm});
            skLineSegment(sketch, "E206", {"start": v(1.27, 22.16) * mm, "end": v(1.27, 20) * mm});
            skLineSegment(sketch, "E207", {"start": v(1.27, 20) * mm, "end": v(2.92, 20) * mm});
            skLineSegment(sketch, "E208", {"start": v(2.92, 20) * mm, "end": v(2.92, 20.51) * mm});
            skLineSegment(sketch, "E209", {"start": v(8.82, 21.64) * mm, "end": v(8.82, 22.16) * mm});
            skLineSegment(sketch, "E210", {"start": v(8.82, 22.16) * mm, "end": v(7.17, 22.16) * mm});
            skLineSegment(sketch, "E211", {"start": v(7.17, 22.16) * mm, "end": v(7.17, 20) * mm});
            skLineSegment(sketch, "E212", {"start": v(7.17, 20) * mm, "end": v(8.82, 20) * mm});
            skLineSegment(sketch, "E213", {"start": v(8.82, 20) * mm, "end": v(8.82, 20.51) * mm});
            skLineSegment(sketch, "E214", {"start": v(11.36, 21.64) * mm, "end": v(11.36, 22.16) * mm});
            skLineSegment(sketch, "E215", {"start": v(11.36, 22.16) * mm, "end": v(9.71, 22.16) * mm});
            skLineSegment(sketch, "E216", {"start": v(9.71, 22.16) * mm, "end": v(9.71, 20) * mm});
            skLineSegment(sketch, "E217", {"start": v(9.71, 20) * mm, "end": v(11.36, 20) * mm});
            skLineSegment(sketch, "E218", {"start": v(11.36, 20) * mm, "end": v(11.36, 20.51) * mm});
            skLineSegment(sketch, "E219.bottom", {"start": v(-38.67, -2.3) * mm, "end": v(-37.65, -2.3) * mm});
            skLineSegment(sketch, "E219.top", {"start": v(-38.67, -1.27) * mm, "end": v(-37.65, -1.27) * mm});
            skLineSegment(sketch, "E219.left", {"start": v(-38.67, -2.3) * mm, "end": v(-38.67, -1.27) * mm});
            skLineSegment(sketch, "E219.right", {"start": v(-37.65, -2.3) * mm, "end": v(-37.65, -1.27) * mm});
            skLineSegment(sketch, "E220", {"start": v(-36.77, -2.3) * mm, "end": v(-36.8, -0.6) * mm});
            skLineSegment(sketch, "E221", {"start": v(-39.51, -2.3) * mm, "end": v(-39.51, -0.6) * mm});
            skLineSegment(sketch, "E222", {"start": v(-39.51, -0.6) * mm, "end": v(-36.8, -0.6) * mm});
            skLineSegment(sketch, "E223", {"start": v(-36.77, -2.3) * mm, "end": v(-37.65, -2.3) * mm});
            skLineSegment(sketch, "E224", {"start": v(-38.67, -2.3) * mm, "end": v(-39.51, -2.3) * mm});
            skLineSegment(sketch, "E225.bottom", {"start": v(-25.5, 12.36) * mm, "end": v(-24.37, 12.36) * mm});
            skLineSegment(sketch, "E225.top", {"start": v(-25.5, 11.21) * mm, "end": v(-24.37, 11.21) * mm});
            skLineSegment(sketch, "E225.left", {"start": v(-25.5, 12.36) * mm, "end": v(-25.5, 11.21) * mm});
            skLineSegment(sketch, "E225.right", {"start": v(-24.37, 12.36) * mm, "end": v(-24.37, 11.21) * mm});
            skLineSegment(sketch, "E226.bottom", {"start": v(-22.92, 12.33) * mm, "end": v(-21.78, 12.33) * mm});
            skLineSegment(sketch, "E226.top", {"start": v(-22.92, 11.19) * mm, "end": v(-21.78, 11.19) * mm});
            skLineSegment(sketch, "E226.left", {"start": v(-22.92, 12.33) * mm, "end": v(-22.92, 11.19) * mm});
            skLineSegment(sketch, "E226.right", {"start": v(-21.78, 12.33) * mm, "end": v(-21.78, 11.19) * mm});
            skLineSegment(sketch, "E227.bottom", {"start": v(-20.37, 12.35) * mm, "end": v(-19.22, 12.35) * mm});
            skLineSegment(sketch, "E227.top", {"start": v(-20.37, 11.2) * mm, "end": v(-19.22, 11.2) * mm});
            skLineSegment(sketch, "E227.left", {"start": v(-20.37, 12.35) * mm, "end": v(-20.37, 11.2) * mm});
            skLineSegment(sketch, "E227.right", {"start": v(-19.22, 12.35) * mm, "end": v(-19.22, 11.2) * mm});
            skLineSegment(sketch, "E228.bottom", {"start": v(-20.37, 9.85) * mm, "end": v(-19.22, 9.85) * mm});
            skLineSegment(sketch, "E228.top", {"start": v(-20.37, 8.71) * mm, "end": v(-19.22, 8.71) * mm});
            skLineSegment(sketch, "E228.left", {"start": v(-20.37, 9.85) * mm, "end": v(-20.37, 8.71) * mm});
            skLineSegment(sketch, "E228.right", {"start": v(-19.22, 9.85) * mm, "end": v(-19.22, 8.71) * mm});
            skLineSegment(sketch, "E229.bottom", {"start": v(-22.89, 9.82) * mm, "end": v(-21.75, 9.82) * mm});
            skLineSegment(sketch, "E229.top", {"start": v(-22.89, 8.68) * mm, "end": v(-21.75, 8.68) * mm});
            skLineSegment(sketch, "E229.left", {"start": v(-22.89, 9.82) * mm, "end": v(-22.89, 8.68) * mm});
            skLineSegment(sketch, "E229.right", {"start": v(-21.75, 9.82) * mm, "end": v(-21.75, 8.68) * mm});
            skLineSegment(sketch, "E230.bottom", {"start": v(-25.42, 9.84) * mm, "end": v(-24.28, 9.84) * mm});
            skLineSegment(sketch, "E230.top", {"start": v(-25.42, 8.7) * mm, "end": v(-24.28, 8.7) * mm});
            skLineSegment(sketch, "E230.left", {"start": v(-25.42, 9.84) * mm, "end": v(-25.42, 8.7) * mm});
            skLineSegment(sketch, "E230.right", {"start": v(-24.28, 9.84) * mm, "end": v(-24.28, 8.7) * mm});
            skLineSegment(sketch, "E231.bottom", {"start": v(-25.4, 7.34) * mm, "end": v(-24.25, 7.34) * mm});
            skLineSegment(sketch, "E231.top", {"start": v(-25.4, 6.2) * mm, "end": v(-24.25, 6.2) * mm});
            skLineSegment(sketch, "E231.left", {"start": v(-25.4, 7.34) * mm, "end": v(-25.4, 6.2) * mm});
            skLineSegment(sketch, "E231.right", {"start": v(-24.25, 7.34) * mm, "end": v(-24.25, 6.2) * mm});
            skLineSegment(sketch, "E232.bottom", {"start": v(-22.9, 7.33) * mm, "end": v(-21.76, 7.33) * mm});
            skLineSegment(sketch, "E232.top", {"start": v(-22.9, 6.19) * mm, "end": v(-21.76, 6.19) * mm});
            skLineSegment(sketch, "E232.left", {"start": v(-22.9, 7.33) * mm, "end": v(-22.9, 6.19) * mm});
            skLineSegment(sketch, "E232.right", {"start": v(-21.76, 7.33) * mm, "end": v(-21.76, 6.19) * mm});
            skLineSegment(sketch, "E233.bottom", {"start": v(-20.3, 7.34) * mm, "end": v(-19.16, 7.34) * mm});
            skLineSegment(sketch, "E233.top", {"start": v(-20.3, 6.2) * mm, "end": v(-19.16, 6.2) * mm});
            skLineSegment(sketch, "E233.left", {"start": v(-20.3, 7.34) * mm, "end": v(-20.3, 6.2) * mm});
            skLineSegment(sketch, "E233.right", {"start": v(-19.16, 7.34) * mm, "end": v(-19.16, 6.2) * mm});
            skLineSegment(sketch, "E234.bottom", {"start": v(-34.63, 15.92) * mm, "end": v(-33.49, 15.92) * mm});
            skLineSegment(sketch, "E234.top", {"start": v(-34.63, 14.78) * mm, "end": v(-33.49, 14.78) * mm});
            skLineSegment(sketch, "E234.left", {"start": v(-34.63, 15.92) * mm, "end": v(-34.63, 14.78) * mm});
            skLineSegment(sketch, "E234.right", {"start": v(-33.49, 15.92) * mm, "end": v(-33.49, 14.78) * mm});
            skLineSegment(sketch, "E235.bottom", {"start": v(-40.58, 15.88) * mm, "end": v(-39.43, 15.88) * mm});
            skLineSegment(sketch, "E235.top", {"start": v(-40.58, 14.74) * mm, "end": v(-39.43, 14.74) * mm});
            skLineSegment(sketch, "E235.left", {"start": v(-40.58, 15.88) * mm, "end": v(-40.58, 14.74) * mm});
            skLineSegment(sketch, "E235.right", {"start": v(-39.43, 15.88) * mm, "end": v(-39.43, 14.74) * mm});
            skLineSegment(sketch, "E236.bottom", {"start": v(-34.3, 4.14) * mm, "end": v(-33.15, 4.14) * mm});
            skLineSegment(sketch, "E236.top", {"start": v(-34.3, 3) * mm, "end": v(-33.15, 3) * mm});
            skLineSegment(sketch, "E236.left", {"start": v(-34.3, 4.14) * mm, "end": v(-34.3, 3) * mm});
            skLineSegment(sketch, "E236.right", {"start": v(-33.15, 4.14) * mm, "end": v(-33.15, 3) * mm});
            skLineSegment(sketch, "E237.bottom", {"start": v(-40.66, 4.12) * mm, "end": v(-39.52, 4.12) * mm});
            skLineSegment(sketch, "E237.top", {"start": v(-40.66, 2.98) * mm, "end": v(-39.52, 2.98) * mm});
            skLineSegment(sketch, "E237.left", {"start": v(-40.66, 4.12) * mm, "end": v(-40.66, 2.98) * mm});
            skLineSegment(sketch, "E237.right", {"start": v(-39.52, 4.12) * mm, "end": v(-39.52, 2.98) * mm});
            skLineSegment(sketch, "E238.bottom", {"start": v(-28.75, 0.6) * mm, "end": v(-27.6, 0.6) * mm});
            skLineSegment(sketch, "E238.top", {"start": v(-28.75, -0.55) * mm, "end": v(-27.6, -0.55) * mm});
            skLineSegment(sketch, "E238.left", {"start": v(-28.75, 0.6) * mm, "end": v(-28.75, -0.55) * mm});
            skLineSegment(sketch, "E238.right", {"start": v(-27.6, 0.6) * mm, "end": v(-27.6, -0.55) * mm});
            skLineSegment(sketch, "E239.bottom", {"start": v(-26.45, 0.18) * mm, "end": v(-25.3, 0.18) * mm});
            skLineSegment(sketch, "E239.top", {"start": v(-26.45, -0.96) * mm, "end": v(-25.3, -0.96) * mm});
            skLineSegment(sketch, "E239.left", {"start": v(-26.45, 0.18) * mm, "end": v(-26.45, -0.96) * mm});
            skLineSegment(sketch, "E239.right", {"start": v(-25.3, 0.18) * mm, "end": v(-25.3, -0.96) * mm});
            skLineSegment(sketch, "E240.bottom", {"start": v(-32.39, -1.02) * mm, "end": v(-31.24, -1.02) * mm});
            skLineSegment(sketch, "E240.top", {"start": v(-32.39, -2.17) * mm, "end": v(-31.24, -2.17) * mm});
            skLineSegment(sketch, "E240.left", {"start": v(-32.39, -1.02) * mm, "end": v(-32.39, -2.17) * mm});
            skLineSegment(sketch, "E240.right", {"start": v(-31.24, -1.02) * mm, "end": v(-31.24, -2.17) * mm});
            skLineSegment(sketch, "E241.bottom", {"start": v(-32.44, -4.74) * mm, "end": v(-31.3, -4.74) * mm});
            skLineSegment(sketch, "E241.top", {"start": v(-32.44, -5.89) * mm, "end": v(-31.3, -5.89) * mm});
            skLineSegment(sketch, "E241.left", {"start": v(-32.44, -4.74) * mm, "end": v(-32.44, -5.89) * mm});
            skLineSegment(sketch, "E241.right", {"start": v(-31.3, -4.74) * mm, "end": v(-31.3, -5.89) * mm});
            skLineSegment(sketch, "E242.bottom", {"start": v(-40.37, -8.62) * mm, "end": v(-39.23, -8.62) * mm});
            skLineSegment(sketch, "E242.top", {"start": v(-40.37, -9.77) * mm, "end": v(-39.23, -9.77) * mm});
            skLineSegment(sketch, "E242.left", {"start": v(-40.37, -8.62) * mm, "end": v(-40.37, -9.77) * mm});
            skLineSegment(sketch, "E242.right", {"start": v(-39.23, -8.62) * mm, "end": v(-39.23, -9.77) * mm});
            skLineSegment(sketch, "E243.bottom", {"start": v(-34.86, -8.63) * mm, "end": v(-33.72, -8.63) * mm});
            skLineSegment(sketch, "E243.top", {"start": v(-34.86, -9.77) * mm, "end": v(-33.72, -9.77) * mm});
            skLineSegment(sketch, "E243.left", {"start": v(-34.86, -8.63) * mm, "end": v(-34.86, -9.77) * mm});
            skLineSegment(sketch, "E243.right", {"start": v(-33.72, -8.63) * mm, "end": v(-33.72, -9.77) * mm});
            skLineSegment(sketch, "E244.bottom", {"start": v(-32.3, -8.59) * mm, "end": v(-31.15, -8.59) * mm});
            skLineSegment(sketch, "E244.top", {"start": v(-32.3, -9.73) * mm, "end": v(-31.15, -9.73) * mm});
            skLineSegment(sketch, "E244.left", {"start": v(-32.3, -8.59) * mm, "end": v(-32.3, -9.73) * mm});
            skLineSegment(sketch, "E244.right", {"start": v(-31.15, -8.59) * mm, "end": v(-31.15, -9.73) * mm});
            skLineSegment(sketch, "E245.bottom", {"start": v(-27.27, -8.73) * mm, "end": v(-26.13, -8.73) * mm});
            skLineSegment(sketch, "E245.top", {"start": v(-27.27, -9.87) * mm, "end": v(-26.13, -9.87) * mm});
            skLineSegment(sketch, "E245.left", {"start": v(-27.27, -8.73) * mm, "end": v(-27.27, -9.87) * mm});
            skLineSegment(sketch, "E245.right", {"start": v(-26.13, -8.73) * mm, "end": v(-26.13, -9.87) * mm});
            skLineSegment(sketch, "E246.bottom", {"start": v(-20.24, -12.03) * mm, "end": v(-19.1, -12.03) * mm});
            skLineSegment(sketch, "E246.top", {"start": v(-20.24, -13.17) * mm, "end": v(-19.1, -13.17) * mm});
            skLineSegment(sketch, "E246.left", {"start": v(-20.24, -12.03) * mm, "end": v(-20.24, -13.17) * mm});
            skLineSegment(sketch, "E246.right", {"start": v(-19.1, -12.03) * mm, "end": v(-19.1, -13.17) * mm});
            skLineSegment(sketch, "E247.bottom", {"start": v(-21.18, -3.64) * mm, "end": v(-20.03, -3.64) * mm});
            skLineSegment(sketch, "E247.top", {"start": v(-21.18, -4.78) * mm, "end": v(-20.03, -4.78) * mm});
            skLineSegment(sketch, "E247.left", {"start": v(-21.18, -3.64) * mm, "end": v(-21.18, -4.78) * mm});
            skLineSegment(sketch, "E247.right", {"start": v(-20.03, -3.64) * mm, "end": v(-20.03, -4.78) * mm});
            skLineSegment(sketch, "E248.bottom", {"start": v(-19.16, -4.54) * mm, "end": v(-18.02, -4.54) * mm});
            skLineSegment(sketch, "E248.top", {"start": v(-19.16, -5.68) * mm, "end": v(-18.02, -5.68) * mm});
            skLineSegment(sketch, "E248.left", {"start": v(-19.16, -4.54) * mm, "end": v(-19.16, -5.68) * mm});
            skLineSegment(sketch, "E248.right", {"start": v(-18.02, -4.54) * mm, "end": v(-18.02, -5.68) * mm});
            skLineSegment(sketch, "E249.bottom", {"start": v(-16.68, -0.85) * mm, "end": v(-15.54, -0.85) * mm});
            skLineSegment(sketch, "E249.top", {"start": v(-16.68, -1.99) * mm, "end": v(-15.54, -1.99) * mm});
            skLineSegment(sketch, "E249.left", {"start": v(-16.68, -0.85) * mm, "end": v(-16.68, -1.99) * mm});
            skLineSegment(sketch, "E249.right", {"start": v(-15.54, -0.85) * mm, "end": v(-15.54, -1.99) * mm});
            skLineSegment(sketch, "E250.bottom", {"start": v(-12.67, -10.88) * mm, "end": v(-11.52, -10.88) * mm});
            skLineSegment(sketch, "E250.top", {"start": v(-12.67, -12.02) * mm, "end": v(-11.52, -12.02) * mm});
            skLineSegment(sketch, "E250.left", {"start": v(-12.67, -10.88) * mm, "end": v(-12.67, -12.02) * mm});
            skLineSegment(sketch, "E250.right", {"start": v(-11.52, -10.88) * mm, "end": v(-11.52, -12.02) * mm});
            skLineSegment(sketch, "E251.bottom", {"start": v(-7.43, -11.15) * mm, "end": v(-6.3, -11.15) * mm});
            skLineSegment(sketch, "E251.top", {"start": v(-7.43, -12.3) * mm, "end": v(-6.3, -12.3) * mm});
            skLineSegment(sketch, "E251.left", {"start": v(-7.43, -11.15) * mm, "end": v(-7.43, -12.3) * mm});
            skLineSegment(sketch, "E251.right", {"start": v(-6.3, -11.15) * mm, "end": v(-6.3, -12.3) * mm});
            skLineSegment(sketch, "E252.bottom", {"start": v(-7.3, -4.77) * mm, "end": v(-6.16, -4.77) * mm});
            skLineSegment(sketch, "E252.top", {"start": v(-7.3, -5.91) * mm, "end": v(-6.16, -5.91) * mm});
            skLineSegment(sketch, "E252.left", {"start": v(-7.3, -4.77) * mm, "end": v(-7.3, -5.91) * mm});
            skLineSegment(sketch, "E252.right", {"start": v(-6.16, -4.77) * mm, "end": v(-6.16, -5.91) * mm});
            skLineSegment(sketch, "E253.bottom", {"start": v(-9.2, 3.97) * mm, "end": v(-8.05, 3.97) * mm});
            skLineSegment(sketch, "E253.top", {"start": v(-9.2, 2.83) * mm, "end": v(-8.05, 2.83) * mm});
            skLineSegment(sketch, "E253.left", {"start": v(-9.2, 3.97) * mm, "end": v(-9.2, 2.83) * mm});
            skLineSegment(sketch, "E253.right", {"start": v(-8.05, 3.97) * mm, "end": v(-8.05, 2.83) * mm});
            skLineSegment(sketch, "E254.bottom", {"start": v(-4.59, 4.08) * mm, "end": v(-3.44, 4.08) * mm});
            skLineSegment(sketch, "E254.top", {"start": v(-4.59, 2.94) * mm, "end": v(-3.44, 2.94) * mm});
            skLineSegment(sketch, "E254.left", {"start": v(-4.59, 4.08) * mm, "end": v(-4.59, 2.94) * mm});
            skLineSegment(sketch, "E254.right", {"start": v(-3.44, 4.08) * mm, "end": v(-3.44, 2.94) * mm});
            skLineSegment(sketch, "E255.bottom", {"start": v(-7.44, 7.69) * mm, "end": v(-6.3, 7.69) * mm});
            skLineSegment(sketch, "E255.top", {"start": v(-7.44, 6.54) * mm, "end": v(-6.3, 6.54) * mm});
            skLineSegment(sketch, "E255.left", {"start": v(-7.44, 7.69) * mm, "end": v(-7.44, 6.54) * mm});
            skLineSegment(sketch, "E255.right", {"start": v(-6.3, 7.69) * mm, "end": v(-6.3, 6.54) * mm});
            skLineSegment(sketch, "E256.bottom", {"start": v(-15.9, 6.02) * mm, "end": v(-14.75, 6.02) * mm});
            skLineSegment(sketch, "E256.top", {"start": v(-15.9, 4.87) * mm, "end": v(-14.75, 4.87) * mm});
            skLineSegment(sketch, "E256.left", {"start": v(-15.9, 6.02) * mm, "end": v(-15.9, 4.87) * mm});
            skLineSegment(sketch, "E256.right", {"start": v(-14.75, 6.02) * mm, "end": v(-14.75, 4.87) * mm});
            skLineSegment(sketch, "E257.bottom", {"start": v(-15.87, 7.69) * mm, "end": v(-14.72, 7.69) * mm});
            skLineSegment(sketch, "E257.top", {"start": v(-15.87, 6.54) * mm, "end": v(-14.72, 6.54) * mm});
            skLineSegment(sketch, "E257.left", {"start": v(-15.87, 7.69) * mm, "end": v(-15.87, 6.54) * mm});
            skLineSegment(sketch, "E257.right", {"start": v(-14.72, 7.69) * mm, "end": v(-14.72, 6.54) * mm});
            skLineSegment(sketch, "E258.bottom", {"start": v(-15.87, 9.54) * mm, "end": v(-14.73, 9.54) * mm});
            skLineSegment(sketch, "E258.top", {"start": v(-15.87, 8.4) * mm, "end": v(-14.73, 8.4) * mm});
            skLineSegment(sketch, "E258.left", {"start": v(-15.87, 9.54) * mm, "end": v(-15.87, 8.4) * mm});
            skLineSegment(sketch, "E258.right", {"start": v(-14.73, 9.54) * mm, "end": v(-14.73, 8.4) * mm});
            skLineSegment(sketch, "E259.bottom", {"start": v(-6.06, 11.4) * mm, "end": v(-4.92, 11.4) * mm});
            skLineSegment(sketch, "E259.top", {"start": v(-6.06, 10.26) * mm, "end": v(-4.92, 10.26) * mm});
            skLineSegment(sketch, "E259.left", {"start": v(-6.06, 11.4) * mm, "end": v(-6.06, 10.26) * mm});
            skLineSegment(sketch, "E259.right", {"start": v(-4.92, 11.4) * mm, "end": v(-4.92, 10.26) * mm});
            skLineSegment(sketch, "E260.bottom", {"start": v(-7.05, 13.03) * mm, "end": v(-5.91, 13.03) * mm});
            skLineSegment(sketch, "E260.top", {"start": v(-7.05, 11.88) * mm, "end": v(-5.91, 11.88) * mm});
            skLineSegment(sketch, "E260.left", {"start": v(-7.05, 13.03) * mm, "end": v(-7.05, 11.88) * mm});
            skLineSegment(sketch, "E260.right", {"start": v(-5.91, 13.03) * mm, "end": v(-5.91, 11.88) * mm});
            skLineSegment(sketch, "E261.bottom", {"start": v(-6.07, 14.62) * mm, "end": v(-4.92, 14.62) * mm});
            skLineSegment(sketch, "E261.top", {"start": v(-6.07, 13.48) * mm, "end": v(-4.92, 13.48) * mm});
            skLineSegment(sketch, "E261.left", {"start": v(-6.07, 14.62) * mm, "end": v(-6.07, 13.48) * mm});
            skLineSegment(sketch, "E261.right", {"start": v(-4.92, 14.62) * mm, "end": v(-4.92, 13.48) * mm});
            skLineSegment(sketch, "E262.bottom", {"start": v(-9.3, 15.98) * mm, "end": v(-8.15, 15.98) * mm});
            skLineSegment(sketch, "E262.top", {"start": v(-9.3, 14.84) * mm, "end": v(-8.15, 14.84) * mm});
            skLineSegment(sketch, "E262.left", {"start": v(-9.3, 15.98) * mm, "end": v(-9.3, 14.84) * mm});
            skLineSegment(sketch, "E262.right", {"start": v(-8.15, 15.98) * mm, "end": v(-8.15, 14.84) * mm});
            skLineSegment(sketch, "E263.bottom", {"start": v(-6.93, 18.1) * mm, "end": v(-5.8, 18.1) * mm});
            skLineSegment(sketch, "E263.top", {"start": v(-6.93, 16.96) * mm, "end": v(-5.8, 16.96) * mm});
            skLineSegment(sketch, "E263.left", {"start": v(-6.93, 18.1) * mm, "end": v(-6.93, 16.96) * mm});
            skLineSegment(sketch, "E263.right", {"start": v(-5.8, 18.1) * mm, "end": v(-5.8, 16.96) * mm});
            skLineSegment(sketch, "E264.bottom", {"start": v(-0.74, 9.54) * mm, "end": v(0.4, 9.54) * mm});
            skLineSegment(sketch, "E264.top", {"start": v(-0.74, 8.4) * mm, "end": v(0.4, 8.4) * mm});
            skLineSegment(sketch, "E264.left", {"start": v(-0.74, 9.54) * mm, "end": v(-0.74, 8.4) * mm});
            skLineSegment(sketch, "E264.right", {"start": v(0.4, 9.54) * mm, "end": v(0.4, 8.4) * mm});
            skLineSegment(sketch, "E265.bottom", {"start": v(0.01, 13.01) * mm, "end": v(1.15, 13.01) * mm});
            skLineSegment(sketch, "E265.top", {"start": v(0.01, 11.87) * mm, "end": v(1.15, 11.87) * mm});
            skLineSegment(sketch, "E265.left", {"start": v(0.01, 13.01) * mm, "end": v(0.01, 11.87) * mm});
            skLineSegment(sketch, "E265.right", {"start": v(1.15, 13.01) * mm, "end": v(1.15, 11.87) * mm});
            skLineSegment(sketch, "E266.bottom", {"start": v(3.11, 9.54) * mm, "end": v(4.26, 9.54) * mm});
            skLineSegment(sketch, "E266.top", {"start": v(3.11, 8.4) * mm, "end": v(4.26, 8.4) * mm});
            skLineSegment(sketch, "E266.left", {"start": v(3.11, 9.54) * mm, "end": v(3.11, 8.4) * mm});
            skLineSegment(sketch, "E266.right", {"start": v(4.26, 9.54) * mm, "end": v(4.26, 8.4) * mm});
            skLineSegment(sketch, "E267.bottom", {"start": v(3.11, 15.88) * mm, "end": v(4.26, 15.88) * mm});
            skLineSegment(sketch, "E267.top", {"start": v(3.11, 14.73) * mm, "end": v(4.26, 14.73) * mm});
            skLineSegment(sketch, "E267.left", {"start": v(3.11, 15.88) * mm, "end": v(3.11, 14.73) * mm});
            skLineSegment(sketch, "E267.right", {"start": v(4.26, 15.88) * mm, "end": v(4.26, 14.73) * mm});
            skLineSegment(sketch, "E268.bottom", {"start": v(3.1, 4.08) * mm, "end": v(4.25, 4.08) * mm});
            skLineSegment(sketch, "E268.top", {"start": v(3.1, 2.94) * mm, "end": v(4.25, 2.94) * mm});
            skLineSegment(sketch, "E268.left", {"start": v(3.1, 4.08) * mm, "end": v(3.1, 2.94) * mm});
            skLineSegment(sketch, "E268.right", {"start": v(4.25, 4.08) * mm, "end": v(4.25, 2.94) * mm});
            skLineSegment(sketch, "E269.bottom", {"start": v(3.1, -2.24) * mm, "end": v(4.25, -2.24) * mm});
            skLineSegment(sketch, "E269.top", {"start": v(3.1, -3.38) * mm, "end": v(4.25, -3.38) * mm});
            skLineSegment(sketch, "E269.left", {"start": v(3.1, -2.24) * mm, "end": v(3.1, -3.38) * mm});
            skLineSegment(sketch, "E269.right", {"start": v(4.25, -2.24) * mm, "end": v(4.25, -3.38) * mm});
            skLineSegment(sketch, "E270.bottom", {"start": v(13.27, -11.17) * mm, "end": v(14.41, -11.17) * mm});
            skLineSegment(sketch, "E270.top", {"start": v(13.27, -12.3) * mm, "end": v(14.41, -12.3) * mm});
            skLineSegment(sketch, "E270.left", {"start": v(13.27, -11.17) * mm, "end": v(13.27, -12.3) * mm});
            skLineSegment(sketch, "E270.right", {"start": v(14.41, -11.17) * mm, "end": v(14.41, -12.3) * mm});
            skLineSegment(sketch, "E271.bottom", {"start": v(13.27, -4.77) * mm, "end": v(14.41, -4.77) * mm});
            skLineSegment(sketch, "E271.top", {"start": v(13.27, -5.91) * mm, "end": v(14.41, -5.91) * mm});
            skLineSegment(sketch, "E271.left", {"start": v(13.27, -4.77) * mm, "end": v(13.27, -5.91) * mm});
            skLineSegment(sketch, "E271.right", {"start": v(14.41, -4.77) * mm, "end": v(14.41, -5.91) * mm});
            skLineSegment(sketch, "E272.bottom", {"start": v(10.83, 11.28) * mm, "end": v(11.97, 11.28) * mm});
            skLineSegment(sketch, "E272.top", {"start": v(10.83, 10.14) * mm, "end": v(11.97, 10.14) * mm});
            skLineSegment(sketch, "E272.left", {"start": v(10.83, 11.28) * mm, "end": v(10.83, 10.14) * mm});
            skLineSegment(sketch, "E272.right", {"start": v(11.97, 11.28) * mm, "end": v(11.97, 10.14) * mm});
            skLineSegment(sketch, "E273.bottom", {"start": v(10.8, 9.54) * mm, "end": v(11.94, 9.54) * mm});
            skLineSegment(sketch, "E273.top", {"start": v(10.8, 8.4) * mm, "end": v(11.94, 8.4) * mm});
            skLineSegment(sketch, "E273.left", {"start": v(10.8, 9.54) * mm, "end": v(10.8, 8.4) * mm});
            skLineSegment(sketch, "E273.right", {"start": v(11.94, 9.54) * mm, "end": v(11.94, 8.4) * mm});
            skLineSegment(sketch, "E274.bottom", {"start": v(15.13, 7.3) * mm, "end": v(16.27, 7.3) * mm});
            skLineSegment(sketch, "E274.top", {"start": v(15.13, 6.17) * mm, "end": v(16.27, 6.17) * mm});
            skLineSegment(sketch, "E274.left", {"start": v(15.13, 7.3) * mm, "end": v(15.13, 6.17) * mm});
            skLineSegment(sketch, "E274.right", {"start": v(16.27, 7.3) * mm, "end": v(16.27, 6.17) * mm});
            skLineSegment(sketch, "E275.bottom", {"start": v(17.73, 7.3) * mm, "end": v(18.88, 7.3) * mm});
            skLineSegment(sketch, "E275.top", {"start": v(17.73, 6.16) * mm, "end": v(18.88, 6.16) * mm});
            skLineSegment(sketch, "E275.left", {"start": v(17.73, 7.3) * mm, "end": v(17.73, 6.16) * mm});
            skLineSegment(sketch, "E275.right", {"start": v(18.88, 7.3) * mm, "end": v(18.88, 6.16) * mm});
            skLineSegment(sketch, "E276.bottom", {"start": v(20.22, 7.31) * mm, "end": v(21.36, 7.31) * mm});
            skLineSegment(sketch, "E276.top", {"start": v(20.22, 6.17) * mm, "end": v(21.36, 6.17) * mm});
            skLineSegment(sketch, "E276.left", {"start": v(20.22, 7.31) * mm, "end": v(20.22, 6.17) * mm});
            skLineSegment(sketch, "E276.right", {"start": v(21.36, 7.31) * mm, "end": v(21.36, 6.17) * mm});
            skLineSegment(sketch, "E277.bottom", {"start": v(20.24, 9.79) * mm, "end": v(21.38, 9.79) * mm});
            skLineSegment(sketch, "E277.top", {"start": v(20.24, 8.64) * mm, "end": v(21.38, 8.64) * mm});
            skLineSegment(sketch, "E277.left", {"start": v(20.24, 9.79) * mm, "end": v(20.24, 8.64) * mm});
            skLineSegment(sketch, "E277.right", {"start": v(21.38, 9.79) * mm, "end": v(21.38, 8.64) * mm});
            skLineSegment(sketch, "E278.bottom", {"start": v(17.74, 9.79) * mm, "end": v(18.88, 9.79) * mm});
            skLineSegment(sketch, "E278.top", {"start": v(17.74, 8.64) * mm, "end": v(18.88, 8.64) * mm});
            skLineSegment(sketch, "E278.left", {"start": v(17.74, 9.79) * mm, "end": v(17.74, 8.64) * mm});
            skLineSegment(sketch, "E278.right", {"start": v(18.88, 9.79) * mm, "end": v(18.88, 8.64) * mm});
            skLineSegment(sketch, "E279.bottom", {"start": v(15.14, 9.78) * mm, "end": v(16.28, 9.78) * mm});
            skLineSegment(sketch, "E279.top", {"start": v(15.14, 8.64) * mm, "end": v(16.28, 8.64) * mm});
            skLineSegment(sketch, "E279.left", {"start": v(15.14, 9.78) * mm, "end": v(15.14, 8.64) * mm});
            skLineSegment(sketch, "E279.right", {"start": v(16.28, 9.78) * mm, "end": v(16.28, 8.64) * mm});
            skLineSegment(sketch, "E280.bottom", {"start": v(15.13, 12.4) * mm, "end": v(16.27, 12.4) * mm});
            skLineSegment(sketch, "E280.top", {"start": v(15.13, 11.25) * mm, "end": v(16.27, 11.25) * mm});
            skLineSegment(sketch, "E280.left", {"start": v(15.13, 12.4) * mm, "end": v(15.13, 11.25) * mm});
            skLineSegment(sketch, "E280.right", {"start": v(16.27, 12.4) * mm, "end": v(16.27, 11.25) * mm});
            skLineSegment(sketch, "E281.bottom", {"start": v(17.74, 12.4) * mm, "end": v(18.89, 12.4) * mm});
            skLineSegment(sketch, "E281.top", {"start": v(17.74, 11.25) * mm, "end": v(18.89, 11.25) * mm});
            skLineSegment(sketch, "E281.left", {"start": v(17.74, 12.4) * mm, "end": v(17.74, 11.25) * mm});
            skLineSegment(sketch, "E281.right", {"start": v(18.89, 12.4) * mm, "end": v(18.89, 11.25) * mm});
            skLineSegment(sketch, "E282.bottom", {"start": v(20.22, 12.4) * mm, "end": v(21.36, 12.4) * mm});
            skLineSegment(sketch, "E282.top", {"start": v(20.22, 11.25) * mm, "end": v(21.36, 11.25) * mm});
            skLineSegment(sketch, "E282.left", {"start": v(20.22, 12.4) * mm, "end": v(20.22, 11.25) * mm});
            skLineSegment(sketch, "E282.right", {"start": v(21.36, 12.4) * mm, "end": v(21.36, 11.25) * mm});
            skSolve(sketch);
        }
        {
            var Q0;
            Q0=makeQuery(id+"F0.imprint","IMPRINT",FACE,{"disambiguationData":[TD([[makeQuery(id+"F0.imprint","IMPRINT",EDGE,{"derivedFrom":sQuery(id+"F0.wireOp",EDGE,"E250.bottom")}),-1.0]])]});
            var Q1;
            Q1=makeQuery(id+"F0.imprint","IMPRINT",FACE,{"disambiguationData":[TD([[makeQuery(id+"F0.imprint","IMPRINT",EDGE,{"derivedFrom":sQuery(id+"F0.wireOp",EDGE,"E266.bottom")}),-1.0]])]});
            var Q2;
            Q2=makeQuery(id+"F0.imprint","IMPRINT",FACE,{"disambiguationData":[TD([[makeQuery(id+"F0.imprint","IMPRINT",EDGE,{"derivedFrom":sQuery(id+"F0.wireOp",EDGE,"E282.bottom")}),-1.0]])]});
            var Q3;
            Q3=makeQuery(id+"F0.imprint","IMPRINT",FACE,{"disambiguationData":[TD([[makeQuery(id+"F0.imprint","IMPRINT",EDGE,{"derivedFrom":sQuery(id+"F0.wireOp",EDGE,"E264.bottom")}),-1.0]])]});
            var Q4;
            Q4=makeQuery(id+"F0.imprint","IMPRINT",FACE,{"disambiguationData":[TD([[makeQuery(id+"F0.imprint","IMPRINT",EDGE,{"derivedFrom":sQuery(id+"F0.wireOp",EDGE,"E280.bottom")}),-1.0]])]});
            var Q5;
            Q5=makeQuery(id+"F0.imprint","IMPRINT",FACE,{"disambiguationData":[TD([[makeQuery(id+"F0.imprint","IMPRINT",EDGE,{"derivedFrom":sQuery(id+"F0.wireOp",EDGE,"E249.bottom")}),-1.0]])]});
            var Q6;
            Q6=makeQuery(id+"F0.imprint","IMPRINT",FACE,{"disambiguationData":[TD([[makeQuery(id+"F0.imprint","IMPRINT",EDGE,{"derivedFrom":sQuery(id+"F0.wireOp",EDGE,"E265.bottom")}),-1.0]])]});
            var Q7;
            Q7=makeQuery(id+"F0.imprint","IMPRINT",FACE,{"disambiguationData":[TD([[makeQuery(id+"F0.imprint","IMPRINT",EDGE,{"derivedFrom":sQuery(id+"F0.wireOp",EDGE,"E235.bottom")}),-1.0]])]});
            var Q8;
            Q8=makeQuery(id+"F0.imprint","IMPRINT",FACE,{"disambiguationData":[TD([[makeQuery(id+"F0.imprint","IMPRINT",EDGE,{"derivedFrom":sQuery(id+"F0.wireOp",EDGE,"E267.bottom")}),-1.0]])]});
            var Q9;
            Q9=makeQuery(id+"F0.imprint","IMPRINT",FACE,{"disambiguationData":[TD([[makeQuery(id+"F0.imprint","IMPRINT",EDGE,{"derivedFrom":sQuery(id+"F0.wireOp",EDGE,"E252.bottom")}),-1.0]])]});
            var Q10;
            Q10=makeQuery(id+"F0.imprint","IMPRINT",FACE,{"disambiguationData":[TD([[makeQuery(id+"F0.imprint","IMPRINT",EDGE,{"derivedFrom":sQuery(id+"F0.wireOp",EDGE,"E269.bottom")}),-1.0]])]});
            var Q11;
            Q11=makeQuery(id+"F0.imprint","IMPRINT",FACE,{"disambiguationData":[TD([[makeQuery(id+"F0.imprint","IMPRINT",EDGE,{"derivedFrom":sQuery(id+"F0.wireOp",EDGE,"E239.bottom")}),-1.0]])]});
            var Q12;
            Q12=makeQuery(id+"F0.imprint","IMPRINT",FACE,{"disambiguationData":[TD([[makeQuery(id+"F0.imprint","IMPRINT",EDGE,{"derivedFrom":sQuery(id+"F0.wireOp",EDGE,"E255.bottom")}),-1.0]])]});
            var Q13;
            Q13=makeQuery(id+"F0.imprint","IMPRINT",FACE,{"disambiguationData":[TD([[makeQuery(id+"F0.imprint","IMPRINT",EDGE,{"derivedFrom":sQuery(id+"F0.wireOp",EDGE,"E271.bottom")}),-1.0]])]});
            var Q14;
            Q14=makeQuery(id+"F0.imprint","IMPRINT",FACE,{"disambiguationData":[TD([[makeQuery(id+"F0.imprint","IMPRINT",EDGE,{"derivedFrom":sQuery(id+"F0.wireOp",EDGE,"E240.bottom")}),-1.0]])]});
            var Q15;
            Q15=makeQuery(id+"F0.imprint","IMPRINT",FACE,{"disambiguationData":[TD([[makeQuery(id+"F0.imprint","IMPRINT",EDGE,{"derivedFrom":sQuery(id+"F0.wireOp",EDGE,"E241.bottom")}),-1.0]])]});
            var Q16;
            Q16=makeQuery(id+"F0.imprint","IMPRINT",FACE,{"disambiguationData":[TD([[makeQuery(id+"F0.imprint","IMPRINT",EDGE,{"derivedFrom":sQuery(id+"F0.wireOp",EDGE,"E258.bottom")}),-1.0]])]});
            var Q17;
            Q17=makeQuery(id+"F0.imprint","IMPRINT",FACE,{"disambiguationData":[TD([[makeQuery(id+"F0.imprint","IMPRINT",EDGE,{"derivedFrom":sQuery(id+"F0.wireOp",EDGE,"E245.bottom")}),-1.0]])]});
            var Q18;
            Q18=makeQuery(id+"F0.imprint","IMPRINT",FACE,{"disambiguationData":[TD([[makeQuery(id+"F0.imprint","IMPRINT",EDGE,{"derivedFrom":sQuery(id+"F0.wireOp",EDGE,"E246.bottom")}),-1.0]])]});
            var Q19;
            Q19=makeQuery(id+"F0.imprint","IMPRINT",FACE,{"disambiguationData":[TD([[makeQuery(id+"F0.imprint","IMPRINT",EDGE,{"derivedFrom":sQuery(id+"F0.wireOp",EDGE,"E247.bottom")}),-1.0]])]});
            var Q20;
            Q20=makeQuery(id+"F0.imprint","IMPRINT",FACE,{"disambiguationData":[TD([[makeQuery(id+"F0.imprint","IMPRINT",EDGE,{"derivedFrom":sQuery(id+"F0.wireOp",EDGE,"E263.bottom")}),-1.0]])]});
            var Q21;
            Q21=makeQuery(id+"F0.imprint","IMPRINT",FACE,{"disambiguationData":[TD([[makeQuery(id+"F0.imprint","IMPRINT",EDGE,{"derivedFrom":sQuery(id+"F0.wireOp",EDGE,"E234.bottom")}),-1.0]])]});
            var Q22;
            Q22=makeQuery(id+"F0.imprint","IMPRINT",FACE,{"disambiguationData":[TD([[makeQuery(id+"F0.imprint","IMPRINT",EDGE,{"derivedFrom":sQuery(id+"F0.wireOp",EDGE,"E225.bottom")}),-1.0]])]});
            var Q23;
            Q23=makeQuery(id+"F0.imprint","IMPRINT",FACE,{"disambiguationData":[TD([[makeQuery(id+"F0.imprint","IMPRINT",EDGE,{"derivedFrom":sQuery(id+"F0.wireOp",EDGE,"E281.bottom")}),-1.0]])]});
            var Q24;
            Q24=makeQuery(id+"F0.imprint","IMPRINT",FACE,{"disambiguationData":[TD([[makeQuery(id+"F0.imprint","IMPRINT",EDGE,{"derivedFrom":sQuery(id+"F0.wireOp",EDGE,"E251.bottom")}),-1.0]])]});
            var Q25;
            Q25=makeQuery(id+"F0.imprint","IMPRINT",FACE,{"disambiguationData":[TD([[makeQuery(id+"F0.imprint","IMPRINT",EDGE,{"derivedFrom":sQuery(id+"F0.wireOp",EDGE,"E268.bottom")}),-1.0]])]});
            var Q26;
            Q26=makeQuery(id+"F0.imprint","IMPRINT",FACE,{"disambiguationData":[TD([[makeQuery(id+"F0.imprint","IMPRINT",EDGE,{"derivedFrom":sQuery(id+"F0.wireOp",EDGE,"E237.bottom")}),-1.0]])]});
            var Q27;
            Q27=makeQuery(id+"F0.imprint","IMPRINT",FACE,{"disambiguationData":[TD([[makeQuery(id+"F0.imprint","IMPRINT",EDGE,{"derivedFrom":sQuery(id+"F0.wireOp",EDGE,"E253.bottom")}),-1.0]])]});
            var Q28;
            Q28=makeQuery(id+"F0.imprint","IMPRINT",FACE,{"disambiguationData":[TD([[makeQuery(id+"F0.imprint","IMPRINT",EDGE,{"derivedFrom":sQuery(id+"F0.wireOp",EDGE,"E238.bottom")}),-1.0]])]});
            var Q29;
            Q29=makeQuery(id+"F0.imprint","IMPRINT",FACE,{"disambiguationData":[TD([[makeQuery(id+"F0.imprint","IMPRINT",EDGE,{"derivedFrom":sQuery(id+"F0.wireOp",EDGE,"E254.bottom")}),-1.0]])]});
            var Q30;
            Q30=makeQuery(id+"F0.imprint","IMPRINT",FACE,{"disambiguationData":[TD([[makeQuery(id+"F0.imprint","IMPRINT",EDGE,{"derivedFrom":sQuery(id+"F0.wireOp",EDGE,"E270.bottom")}),-1.0]])]});
            var Q31;
            Q31=makeQuery(id+"F0.imprint","IMPRINT",FACE,{"disambiguationData":[TD([[makeQuery(id+"F0.imprint","IMPRINT",EDGE,{"derivedFrom":sQuery(id+"F0.wireOp",EDGE,"E242.bottom")}),-1.0]])]});
            var Q32;
            Q32=makeQuery(id+"F0.imprint","IMPRINT",FACE,{"disambiguationData":[TD([[makeQuery(id+"F0.imprint","IMPRINT",EDGE,{"derivedFrom":sQuery(id+"F0.wireOp",EDGE,"E243.bottom")}),-1.0]])]});
            var Q33;
            Q33=makeQuery(id+"F0.imprint","IMPRINT",FACE,{"disambiguationData":[TD([[makeQuery(id+"F0.imprint","IMPRINT",EDGE,{"derivedFrom":sQuery(id+"F0.wireOp",EDGE,"E279.bottom")}),-1.0]])]});
            var Q34;
            Q34=makeQuery(id+"F0.imprint","IMPRINT",FACE,{"disambiguationData":[TD([[makeQuery(id+"F0.imprint","IMPRINT",EDGE,{"derivedFrom":sQuery(id+"F0.wireOp",EDGE,"E233.bottom")}),-1.0]])]});
            var Q35;
            Q35=makeQuery(id+"F0.imprint","IMPRINT",FACE,{"disambiguationData":[TD([[makeQuery(id+"F0.imprint","IMPRINT",EDGE,{"derivedFrom":sQuery(id+"F0.wireOp",EDGE,"E227.bottom")}),-1.0]])]});
            var Q36;
            Q36=makeQuery(id+"F0.imprint","IMPRINT",FACE,{"disambiguationData":[TD([[makeQuery(id+"F0.imprint","IMPRINT",EDGE,{"derivedFrom":sQuery(id+"F0.wireOp",EDGE,"E229.bottom")}),-1.0]])]});
            var Q37;
            Q37=makeQuery(id+"F0.imprint","IMPRINT",FACE,{"disambiguationData":[TD([[makeQuery(id+"F0.imprint","IMPRINT",EDGE,{"derivedFrom":sQuery(id+"F0.wireOp",EDGE,"E230.bottom")}),-1.0]])]});
            var Q38;
            Q38=makeQuery(id+"F0.imprint","IMPRINT",FACE,{"disambiguationData":[TD([[makeQuery(id+"F0.imprint","IMPRINT",EDGE,{"derivedFrom":sQuery(id+"F0.wireOp",EDGE,"E231.bottom")}),-1.0]])]});
            var Q39;
            Q39=makeQuery(id+"F0.imprint","IMPRINT",FACE,{"disambiguationData":[TD([[makeQuery(id+"F0.imprint","IMPRINT",EDGE,{"derivedFrom":sQuery(id+"F0.wireOp",EDGE,"E248.bottom")}),-1.0]])]});
            var Q40;
            Q40=makeQuery(id+"F0.imprint","IMPRINT",FACE,{"disambiguationData":[TD([[makeQuery(id+"F0.imprint","IMPRINT",EDGE,{"derivedFrom":sQuery(id+"F0.wireOp",EDGE,"E236.bottom")}),-1.0]])]});
            var Q41;
            Q41=makeQuery(id+"F0.imprint","IMPRINT",FACE,{"disambiguationData":[TD([[makeQuery(id+"F0.imprint","IMPRINT",EDGE,{"derivedFrom":sQuery(id+"F0.wireOp",EDGE,"E256.bottom")}),-1.0]])]});
            var Q42;
            Q42=makeQuery(id+"F0.imprint","IMPRINT",FACE,{"disambiguationData":[TD([[makeQuery(id+"F0.imprint","IMPRINT",EDGE,{"derivedFrom":sQuery(id+"F0.wireOp",EDGE,"E272.bottom")}),-1.0]])]});
            var Q43;
            Q43=makeQuery(id+"F0.imprint","IMPRINT",FACE,{"disambiguationData":[TD([[makeQuery(id+"F0.imprint","IMPRINT",EDGE,{"derivedFrom":sQuery(id+"F0.wireOp",EDGE,"E257.bottom")}),-1.0]])]});
            var Q44;
            Q44=makeQuery(id+"F0.imprint","IMPRINT",FACE,{"disambiguationData":[TD([[makeQuery(id+"F0.imprint","IMPRINT",EDGE,{"derivedFrom":sQuery(id+"F0.wireOp",EDGE,"E273.bottom")}),-1.0]])]});
            var Q45;
            Q45=makeQuery(id+"F0.imprint","IMPRINT",FACE,{"disambiguationData":[TD([[makeQuery(id+"F0.imprint","IMPRINT",EDGE,{"derivedFrom":sQuery(id+"F0.wireOp",EDGE,"E13.top")}),1.0]])]});
            var Q46;
            Q46=makeQuery(id+"F0.imprint","IMPRINT",FACE,{"disambiguationData":[TD([[makeQuery(id+"F0.imprint","IMPRINT",EDGE,{"derivedFrom":sQuery(id+"F0.wireOp",EDGE,"E259.bottom")}),-1.0]])]});
            var Q47;
            Q47=makeQuery(id+"F0.imprint","IMPRINT",FACE,{"disambiguationData":[TD([[makeQuery(id+"F0.imprint","IMPRINT",EDGE,{"derivedFrom":sQuery(id+"F0.wireOp",EDGE,"E276.bottom")}),-1.0]])]});
            var Q48;
            Q48=makeQuery(id+"F0.imprint","IMPRINT",FACE,{"disambiguationData":[TD([[makeQuery(id+"F0.imprint","IMPRINT",EDGE,{"derivedFrom":sQuery(id+"F0.wireOp",EDGE,"E261.bottom")}),-1.0]])]});
            var Q49;
            Q49=makeQuery(id+"F0.imprint","IMPRINT",FACE,{"disambiguationData":[TD([[makeQuery(id+"F0.imprint","IMPRINT",EDGE,{"derivedFrom":sQuery(id+"F0.wireOp",EDGE,"E277.bottom")}),-1.0]])]});
            var Q50;
            Q50=makeQuery(id+"F0.imprint","IMPRINT",FACE,{"disambiguationData":[TD([[makeQuery(id+"F0.imprint","IMPRINT",EDGE,{"derivedFrom":sQuery(id+"F0.wireOp",EDGE,"E262.bottom")}),-1.0]])]});
            var Q51;
            Q51=makeQuery(id+"F0.imprint","IMPRINT",FACE,{"disambiguationData":[TD([[makeQuery(id+"F0.imprint","IMPRINT",EDGE,{"derivedFrom":sQuery(id+"F0.wireOp",EDGE,"E226.bottom")}),-1.0]])]});
            var Q52;
            Q52=makeQuery(id+"F0.imprint","IMPRINT",FACE,{"disambiguationData":[TD([[makeQuery(id+"F0.imprint","IMPRINT",EDGE,{"derivedFrom":sQuery(id+"F0.wireOp",EDGE,"E228.bottom")}),-1.0]])]});
            var Q53;
            Q53=makeQuery(id+"F0.imprint","IMPRINT",FACE,{"disambiguationData":[TD([[makeQuery(id+"F0.imprint","IMPRINT",EDGE,{"derivedFrom":sQuery(id+"F0.wireOp",EDGE,"E219.top")}),1.0]])]});
            var Q54;
            Q54=makeQuery(id+"F0.imprint","IMPRINT",FACE,{"disambiguationData":[TD([[makeQuery(id+"F0.imprint","IMPRINT",EDGE,{"derivedFrom":sQuery(id+"F0.wireOp",EDGE,"E274.bottom")}),-1.0]])]});
            var Q55;
            Q55=makeQuery(id+"F0.imprint","IMPRINT",FACE,{"disambiguationData":[TD([[makeQuery(id+"F0.imprint","IMPRINT",EDGE,{"derivedFrom":sQuery(id+"F0.wireOp",EDGE,"E275.bottom")}),-1.0]])]});
            var Q56;
            Q56=makeQuery(id+"F0.imprint","IMPRINT",FACE,{"disambiguationData":[TD([[makeQuery(id+"F0.imprint","IMPRINT",EDGE,{"derivedFrom":sQuery(id+"F0.wireOp",EDGE,"E244.bottom")}),-1.0]])]});
            var Q57;
            Q57=makeQuery(id+"F0.imprint","IMPRINT",FACE,{"disambiguationData":[TD([[makeQuery(id+"F0.imprint","IMPRINT",EDGE,{"derivedFrom":sQuery(id+"F0.wireOp",EDGE,"E260.bottom")}),-1.0]])]});
            var Q58;
            Q58=makeQuery(id+"F0.imprint","IMPRINT",FACE,{"disambiguationData":[TD([[makeQuery(id+"F0.imprint","IMPRINT",EDGE,{"derivedFrom":sQuery(id+"F0.wireOp",EDGE,"E278.bottom")}),-1.0]])]});
            var Q59;
            Q59=makeQuery(id+"F0.imprint","IMPRINT",FACE,{"disambiguationData":[TD([[makeQuery(id+"F0.imprint","IMPRINT",EDGE,{"derivedFrom":sQuery(id+"F0.wireOp",EDGE,"E232.bottom")}),-1.0]])]});
            extrude(context, id + "F1", {"entities" : qUnion([Q0, Q1, Q2, Q3, Q4, Q5, Q6, Q7, Q8, Q9, Q10, Q11, Q12, Q13, Q14, Q15, Q16, Q17, Q18, Q19, Q20, Q21, Q22, Q23, Q24, Q25, Q26, Q27, Q28, Q29, Q30, Q31, Q32, Q33, Q34, Q35, Q36, Q37, Q38, Q39, Q40, Q41, Q42, Q43, Q44, Q45, Q46, Q47, Q48, Q49, Q50, Q51, Q52, Q53, Q54, Q55, Q56, Q57, Q58, Q59]), "depth" : 0.64 * mm, "offsetDistance" : 25.4 * mm});
        }
        {
            var Q0;
            Q0=makeQuery(id+"F0.imprint","IMPRINT",FACE,{"disambiguationData":[TD([[makeQuery(id+"F0.imprint","IMPRINT",EDGE,{"derivedFrom":sQuery(id+"F0.wireOp",EDGE,"E0.bottom")}),-1.0]])]});
            var Q1;
            Q1=makeQuery(id+"F0.imprint","IMPRINT",FACE,{"disambiguationData":[TD([[makeQuery(id+"F0.imprint","IMPRINT",EDGE,{"derivedFrom":sQuery(id+"F0.wireOp",EDGE,"E7")}),-1.0]])]});
            var Q2;
            Q2=makeQuery(id+"F0.imprint","IMPRINT",FACE,{"disambiguationData":[TD([[makeQuery(id+"F0.imprint","IMPRINT",EDGE,{"derivedFrom":sQuery(id+"F0.wireOp",EDGE,"E138.bottom")}),1.0]])]});
            var Q3;
            Q3=makeQuery(id+"F0.imprint","IMPRINT",FACE,{"disambiguationData":[TD([[makeQuery(id+"F0.imprint","IMPRINT",EDGE,{"derivedFrom":sQuery(id+"F0.wireOp",EDGE,"E138.bottom")}),-1.0]])]});
            var Q4;
            Q4=makeQuery(id+"F0.imprint","IMPRINT",FACE,{"disambiguationData":[TD([[makeQuery(id+"F0.imprint","IMPRINT",EDGE,{"derivedFrom":sQuery(id+"F0.wireOp",EDGE,"E131.bottom")}),-1.0]])]});
            var Q5;
            Q5=makeQuery(id+"F0.imprint","IMPRINT",FACE,{"disambiguationData":[TD([[makeQuery(id+"F0.imprint","IMPRINT",EDGE,{"derivedFrom":sQuery(id+"F0.wireOp",EDGE,"E131.bottom")}),1.0]])]});
            var Q6;
            Q6=makeQuery(id+"F0.imprint","IMPRINT",FACE,{"disambiguationData":[TD([[makeQuery(id+"F0.imprint","IMPRINT",EDGE,{"derivedFrom":sQuery(id+"F0.wireOp",EDGE,"E7")}),1.0]])]});
            var Q7;
            Q7=makeQuery(id+"F0.imprint","IMPRINT",FACE,{"disambiguationData":[TD([[makeQuery(id+"F0.imprint","IMPRINT",EDGE,{"derivedFrom":sQuery(id+"F0.wireOp",EDGE,"E130.bottom")}),-1.0]])]});
            var Q8;
            Q8=makeQuery(id+"F0.imprint","IMPRINT",FACE,{"disambiguationData":[TD([[makeQuery(id+"F0.imprint","IMPRINT",EDGE,{"derivedFrom":sQuery(id+"F0.wireOp",EDGE,"E130.bottom")}),1.0]])]});
            var Q9;
            Q9=makeQuery(id+"F0.imprint","IMPRINT",FACE,{"disambiguationData":[TD([[makeQuery(id+"F0.imprint","IMPRINT",EDGE,{"derivedFrom":sQuery(id+"F0.wireOp",EDGE,"E129.bottom")}),1.0]])]});
            var Q10;
            Q10=makeQuery(id+"F0.imprint","IMPRINT",FACE,{"disambiguationData":[TD([[makeQuery(id+"F0.imprint","IMPRINT",EDGE,{"derivedFrom":sQuery(id+"F0.wireOp",EDGE,"E129.bottom")}),-1.0]])]});
            var Q11;
            Q11=makeQuery(id+"F0.imprint","IMPRINT",FACE,{"disambiguationData":[TD([[makeQuery(id+"F0.imprint","IMPRINT",EDGE,{"derivedFrom":sQuery(id+"F0.wireOp",EDGE,"E128.bottom")}),-1.0]])]});
            var Q12;
            Q12=makeQuery(id+"F0.imprint","IMPRINT",FACE,{"disambiguationData":[TD([[makeQuery(id+"F0.imprint","IMPRINT",EDGE,{"derivedFrom":sQuery(id+"F0.wireOp",EDGE,"E128.bottom")}),1.0]])]});
            var Q13;
            Q13=makeQuery(id+"F0.imprint","IMPRINT",FACE,{"disambiguationData":[TD([[makeQuery(id+"F0.imprint","IMPRINT",EDGE,{"derivedFrom":sQuery(id+"F0.wireOp",EDGE,"E127.bottom")}),1.0]])]});
            var Q14;
            Q14=makeQuery(id+"F0.imprint","IMPRINT",FACE,{"disambiguationData":[TD([[makeQuery(id+"F0.imprint","IMPRINT",EDGE,{"derivedFrom":sQuery(id+"F0.wireOp",EDGE,"E127.bottom")}),-1.0]])]});
            var Q15;
            Q15=makeQuery(id+"F0.imprint","IMPRINT",FACE,{"disambiguationData":[TD([[makeQuery(id+"F0.imprint","IMPRINT",EDGE,{"derivedFrom":sQuery(id+"F0.wireOp",EDGE,"E125.bottom")}),-1.0]])]});
            var Q16;
            Q16=makeQuery(id+"F0.imprint","IMPRINT",FACE,{"disambiguationData":[TD([[makeQuery(id+"F0.imprint","IMPRINT",EDGE,{"derivedFrom":sQuery(id+"F0.wireOp",EDGE,"E125.bottom")}),1.0]])]});
            var Q17;
            Q17=makeQuery(id+"F0.imprint","IMPRINT",FACE,{"disambiguationData":[TD([[makeQuery(id+"F0.imprint","IMPRINT",EDGE,{"derivedFrom":sQuery(id+"F0.wireOp",EDGE,"E126.bottom")}),-1.0]])]});
            var Q18;
            Q18=makeQuery(id+"F0.imprint","IMPRINT",FACE,{"disambiguationData":[TD([[makeQuery(id+"F0.imprint","IMPRINT",EDGE,{"derivedFrom":sQuery(id+"F0.wireOp",EDGE,"E126.bottom")}),1.0]])]});
            var Q19;
            Q19=makeQuery(id+"F0.imprint","IMPRINT",FACE,{"disambiguationData":[TD([[makeQuery(id+"F0.imprint","IMPRINT",EDGE,{"derivedFrom":sQuery(id+"F0.wireOp",EDGE,"E124.bottom")}),1.0]])]});
            var Q20;
            Q20=makeQuery(id+"F0.imprint","IMPRINT",FACE,{"disambiguationData":[TD([[makeQuery(id+"F0.imprint","IMPRINT",EDGE,{"derivedFrom":sQuery(id+"F0.wireOp",EDGE,"E123.bottom")}),-1.0]])]});
            var Q21;
            Q21=makeQuery(id+"F0.imprint","IMPRINT",FACE,{"disambiguationData":[TD([[makeQuery(id+"F0.imprint","IMPRINT",EDGE,{"derivedFrom":sQuery(id+"F0.wireOp",EDGE,"E123.bottom")}),1.0]])]});
            var Q22;
            Q22=makeQuery(id+"F0.imprint","IMPRINT",FACE,{"disambiguationData":[TD([[makeQuery(id+"F0.imprint","IMPRINT",EDGE,{"derivedFrom":sQuery(id+"F0.wireOp",EDGE,"E122.bottom")}),-1.0]])]});
            var Q23;
            Q23=makeQuery(id+"F0.imprint","IMPRINT",FACE,{"disambiguationData":[TD([[makeQuery(id+"F0.imprint","IMPRINT",EDGE,{"derivedFrom":sQuery(id+"F0.wireOp",EDGE,"E122.bottom")}),1.0]])]});
            var Q24;
            Q24=makeQuery(id+"F0.imprint","IMPRINT",FACE,{"disambiguationData":[TD([[makeQuery(id+"F0.imprint","IMPRINT",EDGE,{"derivedFrom":sQuery(id+"F0.wireOp",EDGE,"E121.bottom")}),1.0]])]});
            var Q25;
            Q25=makeQuery(id+"F0.imprint","IMPRINT",FACE,{"disambiguationData":[TD([[makeQuery(id+"F0.imprint","IMPRINT",EDGE,{"derivedFrom":sQuery(id+"F0.wireOp",EDGE,"E121.bottom")}),-1.0]])]});
            var Q26;
            Q26=makeQuery(id+"F0.imprint","IMPRINT",FACE,{"disambiguationData":[TD([[makeQuery(id+"F0.imprint","IMPRINT",EDGE,{"derivedFrom":sQuery(id+"F0.wireOp",EDGE,"E124.bottom")}),-1.0]])]});
            var Q27;
            Q27=makeQuery(id+"F0.imprint","IMPRINT",FACE,{"disambiguationData":[TD([[makeQuery(id+"F0.imprint","IMPRINT",EDGE,{"derivedFrom":sQuery(id+"F0.wireOp",EDGE,"E120.bottom")}),-1.0]])]});
            var Q28;
            Q28=makeQuery(id+"F0.imprint","IMPRINT",FACE,{"disambiguationData":[TD([[makeQuery(id+"F0.imprint","IMPRINT",EDGE,{"derivedFrom":sQuery(id+"F0.wireOp",EDGE,"E120.bottom")}),1.0]])]});
            var Q29;
            Q29=makeQuery(id+"F0.imprint","IMPRINT",FACE,{"disambiguationData":[TD([[makeQuery(id+"F0.imprint","IMPRINT",EDGE,{"derivedFrom":sQuery(id+"F0.wireOp",EDGE,"E119.bottom")}),1.0]])]});
            var Q30;
            Q30=makeQuery(id+"F0.imprint","IMPRINT",FACE,{"disambiguationData":[TD([[makeQuery(id+"F0.imprint","IMPRINT",EDGE,{"derivedFrom":sQuery(id+"F0.wireOp",EDGE,"E118.bottom")}),-1.0]])]});
            var Q31;
            Q31=makeQuery(id+"F0.imprint","IMPRINT",FACE,{"disambiguationData":[TD([[makeQuery(id+"F0.imprint","IMPRINT",EDGE,{"derivedFrom":sQuery(id+"F0.wireOp",EDGE,"E118.bottom")}),1.0]])]});
            var Q32;
            Q32=makeQuery(id+"F0.imprint","IMPRINT",FACE,{"disambiguationData":[TD([[makeQuery(id+"F0.imprint","IMPRINT",EDGE,{"derivedFrom":sQuery(id+"F0.wireOp",EDGE,"E119.bottom")}),-1.0]])]});
            var Q33;
            Q33=makeQuery(id+"F0.imprint","IMPRINT",FACE,{"disambiguationData":[TD([[makeQuery(id+"F0.imprint","IMPRINT",EDGE,{"derivedFrom":sQuery(id+"F0.wireOp",EDGE,"E117.bottom")}),-1.0]])]});
            var Q34;
            Q34=makeQuery(id+"F0.imprint","IMPRINT",FACE,{"disambiguationData":[TD([[makeQuery(id+"F0.imprint","IMPRINT",EDGE,{"derivedFrom":sQuery(id+"F0.wireOp",EDGE,"E117.bottom")}),1.0]])]});
            var Q35;
            Q35=makeQuery(id+"F0.imprint","IMPRINT",FACE,{"disambiguationData":[TD([[makeQuery(id+"F0.imprint","IMPRINT",EDGE,{"derivedFrom":sQuery(id+"F0.wireOp",EDGE,"E132.bottom")}),-1.0]])]});
            var Q36;
            Q36=makeQuery(id+"F0.imprint","IMPRINT",FACE,{"disambiguationData":[TD([[makeQuery(id+"F0.imprint","IMPRINT",EDGE,{"derivedFrom":sQuery(id+"F0.wireOp",EDGE,"E132.bottom")}),1.0]])]});
            var Q37;
            Q37=makeQuery(id+"F0.imprint","IMPRINT",FACE,{"disambiguationData":[TD([[makeQuery(id+"F0.imprint","IMPRINT",EDGE,{"derivedFrom":sQuery(id+"F0.wireOp",EDGE,"E5")}),1.0]])]});
            var Q38;
            Q38=makeQuery(id+"F0.imprint","IMPRINT",FACE,{"disambiguationData":[TD([[makeQuery(id+"F0.imprint","IMPRINT",EDGE,{"derivedFrom":sQuery(id+"F0.wireOp",EDGE,"E5")}),-1.0]])]});
            var Q39;
            Q39=makeQuery(id+"F0.imprint","IMPRINT",FACE,{"disambiguationData":[TD([[makeQuery(id+"F0.imprint","IMPRINT",EDGE,{"derivedFrom":sQuery(id+"F0.wireOp",EDGE,"E3")}),1.0]])]});
            var Q40;
            Q40=makeQuery(id+"F0.imprint","IMPRINT",FACE,{"disambiguationData":[TD([[makeQuery(id+"F0.imprint","IMPRINT",EDGE,{"derivedFrom":sQuery(id+"F0.wireOp",EDGE,"E3")}),-1.0]])]});
            var Q41;
            Q41=makeQuery(id+"F0.imprint","IMPRINT",FACE,{"disambiguationData":[TD([[makeQuery(id+"F0.imprint","IMPRINT",EDGE,{"derivedFrom":sQuery(id+"F0.wireOp",EDGE,"E71.bottom")}),-1.0]])]});
            var Q42;
            Q42=makeQuery(id+"F0.imprint","IMPRINT",FACE,{"disambiguationData":[TD([[makeQuery(id+"F0.imprint","IMPRINT",EDGE,{"derivedFrom":sQuery(id+"F0.wireOp",EDGE,"E71.bottom")}),1.0]])]});
            var Q43;
            Q43=makeQuery(id+"F0.imprint","IMPRINT",FACE,{"disambiguationData":[TD([[makeQuery(id+"F0.imprint","IMPRINT",EDGE,{"derivedFrom":sQuery(id+"F0.wireOp",EDGE,"E69.bottom")}),1.0]])]});
            var Q44;
            Q44=makeQuery(id+"F0.imprint","IMPRINT",FACE,{"disambiguationData":[TD([[makeQuery(id+"F0.imprint","IMPRINT",EDGE,{"derivedFrom":sQuery(id+"F0.wireOp",EDGE,"E68.bottom")}),-1.0]])]});
            var Q45;
            Q45=makeQuery(id+"F0.imprint","IMPRINT",FACE,{"disambiguationData":[TD([[makeQuery(id+"F0.imprint","IMPRINT",EDGE,{"derivedFrom":sQuery(id+"F0.wireOp",EDGE,"E68.bottom")}),1.0]])]});
            var Q46;
            Q46=makeQuery(id+"F0.imprint","IMPRINT",FACE,{"disambiguationData":[TD([[makeQuery(id+"F0.imprint","IMPRINT",EDGE,{"derivedFrom":sQuery(id+"F0.wireOp",EDGE,"E67.bottom")}),1.0]])]});
            var Q47;
            Q47=makeQuery(id+"F0.imprint","IMPRINT",FACE,{"disambiguationData":[TD([[makeQuery(id+"F0.imprint","IMPRINT",EDGE,{"derivedFrom":sQuery(id+"F0.wireOp",EDGE,"E69.bottom")}),-1.0]])]});
            var Q48;
            Q48=makeQuery(id+"F0.imprint","IMPRINT",FACE,{"disambiguationData":[TD([[makeQuery(id+"F0.imprint","IMPRINT",EDGE,{"derivedFrom":sQuery(id+"F0.wireOp",EDGE,"E67.bottom")}),-1.0]])]});
            var Q49;
            Q49=makeQuery(id+"F0.imprint","IMPRINT",FACE,{"disambiguationData":[TD([[makeQuery(id+"F0.imprint","IMPRINT",EDGE,{"derivedFrom":sQuery(id+"F0.wireOp",EDGE,"E66.bottom")}),-1.0]])]});
            var Q50;
            Q50=makeQuery(id+"F0.imprint","IMPRINT",FACE,{"disambiguationData":[TD([[makeQuery(id+"F0.imprint","IMPRINT",EDGE,{"derivedFrom":sQuery(id+"F0.wireOp",EDGE,"E66.bottom")}),1.0]])]});
            var Q51;
            Q51=makeQuery(id+"F0.imprint","IMPRINT",FACE,{"disambiguationData":[TD([[makeQuery(id+"F0.imprint","IMPRINT",EDGE,{"derivedFrom":sQuery(id+"F0.wireOp",EDGE,"E65.bottom")}),-1.0]])]});
            var Q52;
            Q52=makeQuery(id+"F0.imprint","IMPRINT",FACE,{"disambiguationData":[TD([[makeQuery(id+"F0.imprint","IMPRINT",EDGE,{"derivedFrom":sQuery(id+"F0.wireOp",EDGE,"E65.bottom")}),1.0]])]});
            var Q53;
            Q53=makeQuery(id+"F0.imprint","IMPRINT",FACE,{"disambiguationData":[TD([[makeQuery(id+"F0.imprint","IMPRINT",EDGE,{"derivedFrom":sQuery(id+"F0.wireOp",EDGE,"E64.bottom")}),1.0]])]});
            var Q54;
            Q54=makeQuery(id+"F0.imprint","IMPRINT",FACE,{"disambiguationData":[TD([[makeQuery(id+"F0.imprint","IMPRINT",EDGE,{"derivedFrom":sQuery(id+"F0.wireOp",EDGE,"E63.bottom")}),-1.0]])]});
            var Q55;
            Q55=makeQuery(id+"F0.imprint","IMPRINT",FACE,{"disambiguationData":[TD([[makeQuery(id+"F0.imprint","IMPRINT",EDGE,{"derivedFrom":sQuery(id+"F0.wireOp",EDGE,"E63.bottom")}),1.0]])]});
            var Q56;
            Q56=makeQuery(id+"F0.imprint","IMPRINT",FACE,{"disambiguationData":[TD([[makeQuery(id+"F0.imprint","IMPRINT",EDGE,{"derivedFrom":sQuery(id+"F0.wireOp",EDGE,"E61.bottom")}),-1.0]])]});
            var Q57;
            Q57=makeQuery(id+"F0.imprint","IMPRINT",FACE,{"disambiguationData":[TD([[makeQuery(id+"F0.imprint","IMPRINT",EDGE,{"derivedFrom":sQuery(id+"F0.wireOp",EDGE,"E25.bottom")}),-1.0]])]});
            var Q58;
            Q58=makeQuery(id+"F0.imprint","IMPRINT",FACE,{"disambiguationData":[TD([[makeQuery(id+"F0.imprint","IMPRINT",EDGE,{"derivedFrom":sQuery(id+"F0.wireOp",EDGE,"E25.bottom")}),1.0]])]});
            var Q59;
            Q59=makeQuery(id+"F0.imprint","IMPRINT",FACE,{"disambiguationData":[TD([[makeQuery(id+"F0.imprint","IMPRINT",EDGE,{"derivedFrom":sQuery(id+"F0.wireOp",EDGE,"E64.bottom")}),-1.0]])]});
            var Q60;
            Q60=makeQuery(id+"F0.imprint","IMPRINT",FACE,{"disambiguationData":[TD([[makeQuery(id+"F0.imprint","IMPRINT",EDGE,{"derivedFrom":sQuery(id+"F0.wireOp",EDGE,"E61.bottom")}),1.0]])]});
            var Q61;
            Q61=makeQuery(id+"F0.imprint","IMPRINT",FACE,{"disambiguationData":[TD([[makeQuery(id+"F0.imprint","IMPRINT",EDGE,{"derivedFrom":sQuery(id+"F0.wireOp",EDGE,"E24.bottom")}),-1.0]])]});
            var Q62;
            Q62=makeQuery(id+"F0.imprint","IMPRINT",FACE,{"disambiguationData":[TD([[makeQuery(id+"F0.imprint","IMPRINT",EDGE,{"derivedFrom":sQuery(id+"F0.wireOp",EDGE,"E24.bottom")}),1.0]])]});
            var Q63;
            Q63=makeQuery(id+"F0.imprint","IMPRINT",FACE,{"disambiguationData":[TD([[makeQuery(id+"F0.imprint","IMPRINT",EDGE,{"derivedFrom":sQuery(id+"F0.wireOp",EDGE,"E23.bottom")}),1.0]])]});
            var Q64;
            Q64=makeQuery(id+"F0.imprint","IMPRINT",FACE,{"disambiguationData":[TD([[makeQuery(id+"F0.imprint","IMPRINT",EDGE,{"derivedFrom":sQuery(id+"F0.wireOp",EDGE,"E22.bottom")}),1.0]])]});
            var Q65;
            Q65=makeQuery(id+"F0.imprint","IMPRINT",FACE,{"disambiguationData":[TD([[makeQuery(id+"F0.imprint","IMPRINT",EDGE,{"derivedFrom":sQuery(id+"F0.wireOp",EDGE,"E22.bottom")}),-1.0]])]});
            var Q66;
            Q66=makeQuery(id+"F0.imprint","IMPRINT",FACE,{"disambiguationData":[TD([[makeQuery(id+"F0.imprint","IMPRINT",EDGE,{"derivedFrom":sQuery(id+"F0.wireOp",EDGE,"E21.bottom")}),-1.0]])]});
            var Q67;
            Q67=makeQuery(id+"F0.imprint","IMPRINT",FACE,{"disambiguationData":[TD([[makeQuery(id+"F0.imprint","IMPRINT",EDGE,{"derivedFrom":sQuery(id+"F0.wireOp",EDGE,"E21.bottom")}),1.0]])]});
            var Q68;
            Q68=makeQuery(id+"F0.imprint","IMPRINT",FACE,{"disambiguationData":[TD([[makeQuery(id+"F0.imprint","IMPRINT",EDGE,{"derivedFrom":sQuery(id+"F0.wireOp",EDGE,"E20.bottom")}),-1.0]])]});
            var Q69;
            Q69=makeQuery(id+"F0.imprint","IMPRINT",FACE,{"disambiguationData":[TD([[makeQuery(id+"F0.imprint","IMPRINT",EDGE,{"derivedFrom":sQuery(id+"F0.wireOp",EDGE,"E20.bottom")}),1.0]])]});
            var Q70;
            Q70=makeQuery(id+"F0.imprint","IMPRINT",FACE,{"disambiguationData":[TD([[makeQuery(id+"F0.imprint","IMPRINT",EDGE,{"derivedFrom":sQuery(id+"F0.wireOp",EDGE,"E18.bottom")}),1.0]])]});
            var Q71;
            Q71=makeQuery(id+"F0.imprint","IMPRINT",FACE,{"disambiguationData":[TD([[makeQuery(id+"F0.imprint","IMPRINT",EDGE,{"derivedFrom":sQuery(id+"F0.wireOp",EDGE,"E18.bottom")}),-1.0]])]});
            var Q72;
            {var subQ0=sQuery(id+"F0.wireOp",EDGE,"E17.bottom");Q72=makeQuery(id+"F0.imprint","IMPRINT",FACE,{"disambiguationData":[TD([[makeQuery(id+"F0.imprint","IMPRINT",EDGE,{"derivedFrom":subQ0}),-1.0]])]});}
            var Q73;
            Q73=makeQuery(id+"F0.imprint","IMPRINT",FACE,{"disambiguationData":[TD([[makeQuery(id+"F0.imprint","IMPRINT",EDGE,{"derivedFrom":sQuery(id+"F0.wireOp",EDGE,"E1")}),-1.0]])]});
            var Q74;
            Q74=makeQuery(id+"F0.imprint","IMPRINT",FACE,{"disambiguationData":[TD([[makeQuery(id+"F0.imprint","IMPRINT",EDGE,{"derivedFrom":sQuery(id+"F0.wireOp",EDGE,"E23.bottom")}),-1.0]])]});
            var Q75;
            {var subQ3=sQuery(id+"F0.wireOp",EDGE,"E17.bottom");Q75=makeQuery(id+"F0.imprint","IMPRINT",FACE,{"disambiguationData":[TD([[makeQuery(id+"F0.imprint","IMPRINT",EDGE,{"derivedFrom":subQ3}),1.0]])]});}
            var Q76;
            Q76=makeQuery(id+"F0.imprint","IMPRINT",FACE,{"disambiguationData":[TD([[makeQuery(id+"F0.imprint","IMPRINT",EDGE,{"derivedFrom":sQuery(id+"F0.wireOp",EDGE,"E1")}),1.0]])]});
            extrude(context, id + "F2", {"entities" : qUnion([Q0, Q1, Q2, Q3, Q4, Q5, Q6, Q7, Q8, Q9, Q10, Q11, Q12, Q13, Q14, Q15, Q16, Q17, Q18, Q19, Q20, Q21, Q22, Q23, Q24, Q25, Q26, Q27, Q28, Q29, Q30, Q31, Q32, Q33, Q34, Q35, Q36, Q37, Q38, Q39, Q40, Q41, Q42, Q43, Q44, Q45, Q46, Q47, Q48, Q49, Q50, Q51, Q52, Q53, Q54, Q55, Q56, Q57, Q58, Q59, Q60, Q61, Q62, Q63, Q64, Q65, Q66, Q67, Q68, Q69, Q70, Q71, Q72, Q73, Q74, Q75, Q76]), "depth" : 0.64 * mm, "offsetDistance" : 25.4 * mm});
        }
    });
